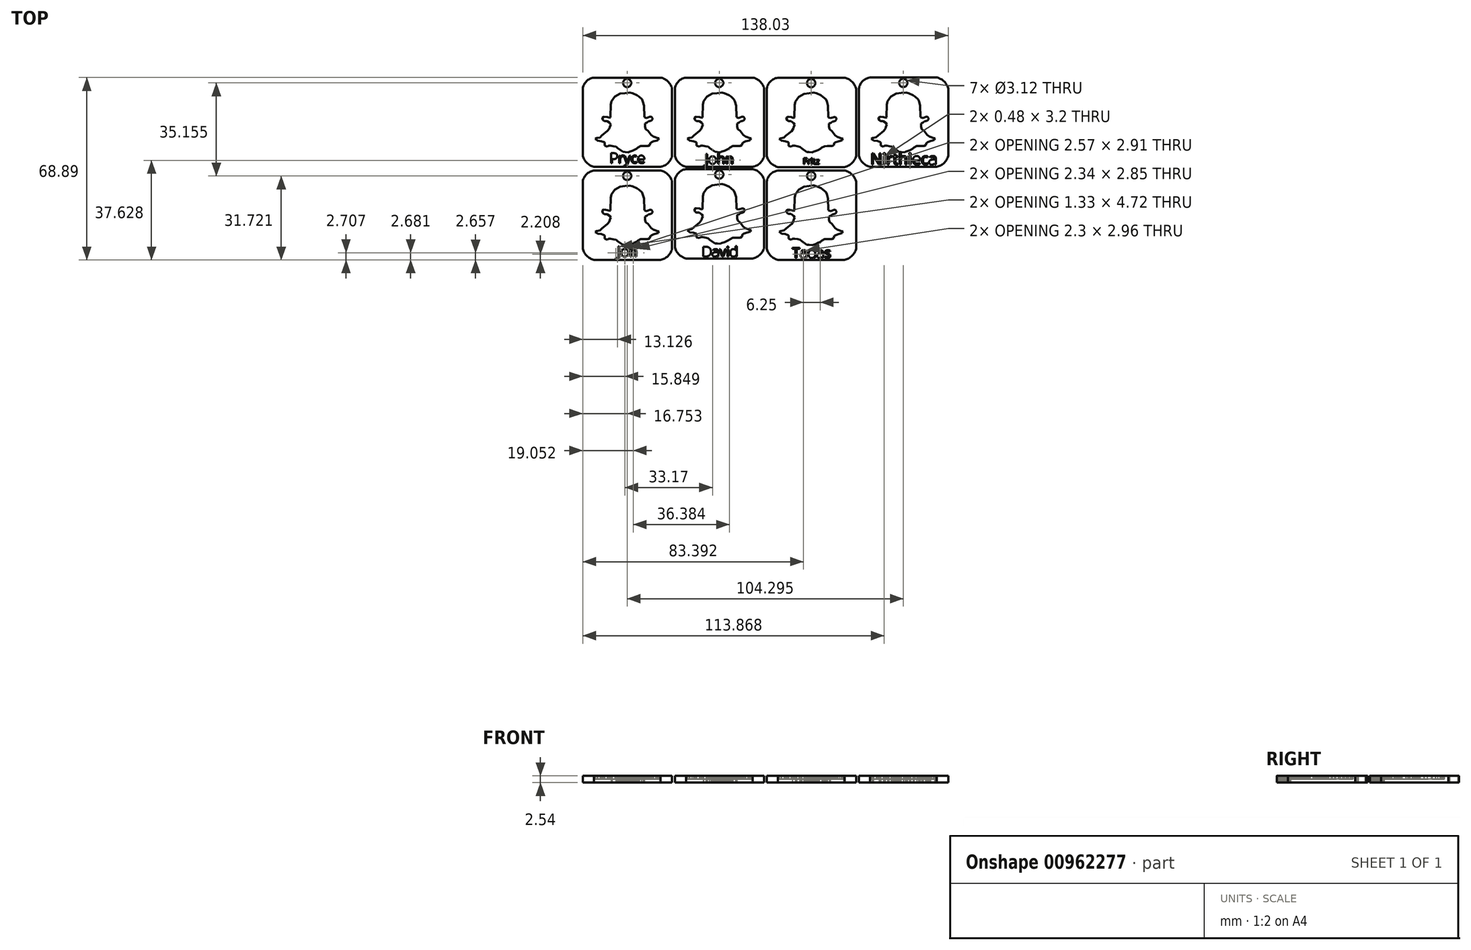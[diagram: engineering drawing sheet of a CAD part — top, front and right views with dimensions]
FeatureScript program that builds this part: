
annotation { "Feature Type Name" : "Feature", "Feature Type Description" : "" }
export const myFeature = defineFeature(function(context is Context, id is Id, definition is map)
    precondition{}
    {
        {
            var Q0;
            Q0=qCreatedBy(makeId("Top.planeOp"),FACE);
            var sketch = newSketch(context, id + "F0", { "sketchPlane" : qUnion([Q0])});
            skPoint(sketch, "E0.middle", {"position": v(-58.3, 36.23) * mm});
            skPoint(sketch, "E1.middle", {"position": v(-58.18, 29.07) * mm});
            skLineSegment(sketch, "E2", {"start": v(-64.66, 30.3) * mm, "end": v(-64.47, 34.86) * mm});
            skLineSegment(sketch, "E3", {"start": v(-64.47, 34.86) * mm, "end": v(-64.28, 36.1) * mm});
            skLineSegment(sketch, "E4", {"start": v(-64.28, 36.1) * mm, "end": v(-62.95, 37.88) * mm});
            skLineSegment(sketch, "E5", {"start": v(-62.95, 37.88) * mm, "end": v(-60.96, 39.02) * mm});
            skLineSegment(sketch, "E6", {"start": v(-60.96, 39.02) * mm, "end": v(-59.1, 39.25) * mm});
            skLineSegment(sketch, "E7", {"start": v(-59.1, 39.25) * mm, "end": v(-57.35, 39.47) * mm});
            skLineSegment(sketch, "E8", {"start": v(-57.35, 39.47) * mm, "end": v(-56.3, 39.2) * mm});
            skLineSegment(sketch, "E9", {"start": v(-56.3, 39.2) * mm, "end": v(-54.6, 38.45) * mm});
            skLineSegment(sketch, "E10", {"start": v(-54.6, 38.45) * mm, "end": v(-53.83, 37.88) * mm});
            skLineSegment(sketch, "E11", {"start": v(-53.83, 37.88) * mm, "end": v(-52.74, 36.93) * mm});
            skLineSegment(sketch, "E12", {"start": v(-52.74, 36.93) * mm, "end": v(-52.36, 36.1) * mm});
            skLineSegment(sketch, "E13", {"start": v(-52.36, 36.1) * mm, "end": v(-51.94, 34.53) * mm});
            skLineSegment(sketch, "E14", {"start": v(-51.94, 34.53) * mm, "end": v(-51.94, 33.03) * mm});
            skLineSegment(sketch, "E15", {"start": v(-51.94, 33.03) * mm, "end": v(-51.84, 31.8) * mm});
            skLineSegment(sketch, "E16", {"start": v(-51.84, 31.8) * mm, "end": v(-51.84, 30.61) * mm});
            skLineSegment(sketch, "E17", {"start": v(-51.84, 30.61) * mm, "end": v(-51.84, 30.14) * mm});
            skLineSegment(sketch, "E18", {"start": v(-51.84, 30.14) * mm, "end": v(-50.99, 29.8) * mm});
            skLineSegment(sketch, "E19", {"start": v(-50.99, 29.8) * mm, "end": v(-49.7, 30.28) * mm});
            skLineSegment(sketch, "E20", {"start": v(-49.7, 30.28) * mm, "end": v(-49.18, 30.28) * mm});
            skLineSegment(sketch, "E21", {"start": v(-49.18, 30.28) * mm, "end": v(-48.8, 29.8) * mm});
            skLineSegment(sketch, "E22", {"start": v(-48.8, 29.8) * mm, "end": v(-48.8, 29.3) * mm});
            skLineSegment(sketch, "E23", {"start": v(-48.8, 29.3) * mm, "end": v(-49.14, 28.9) * mm});
            skLineSegment(sketch, "E24", {"start": v(-49.14, 28.9) * mm, "end": v(-49.73, 28.63) * mm});
            skLineSegment(sketch, "E25", {"start": v(-49.73, 28.63) * mm, "end": v(-50.14, 28.63) * mm});
            skLineSegment(sketch, "E26", {"start": v(-50.14, 28.63) * mm, "end": v(-50.82, 28.13) * mm});
            skLineSegment(sketch, "E27", {"start": v(-50.82, 28.13) * mm, "end": v(-51.57, 27.77) * mm});
            skLineSegment(sketch, "E28", {"start": v(-51.57, 27.77) * mm, "end": v(-51.57, 27.21) * mm});
            skLineSegment(sketch, "E29", {"start": v(-51.57, 27.21) * mm, "end": v(-51.57, 26.48) * mm});
            skLineSegment(sketch, "E30", {"start": v(-51.57, 26.48) * mm, "end": v(-51.28, 25.62) * mm});
            skLineSegment(sketch, "E31", {"start": v(-51.28, 25.62) * mm, "end": v(-50.37, 24.96) * mm});
            skLineSegment(sketch, "E32", {"start": v(-50.37, 24.96) * mm, "end": v(-49.26, 23.43) * mm});
            skLineSegment(sketch, "E33", {"start": v(-49.26, 23.43) * mm, "end": v(-48.4, 22.8) * mm});
            skLineSegment(sketch, "E34", {"start": v(-48.4, 22.8) * mm, "end": v(-47.65, 22.5) * mm});
            skLineSegment(sketch, "E35", {"start": v(-47.65, 22.5) * mm, "end": v(-46.73, 22.16) * mm});
            skLineSegment(sketch, "E36", {"start": v(-46.73, 22.16) * mm, "end": v(-46.2, 22.16) * mm});
            skLineSegment(sketch, "E37", {"start": v(-46.2, 22.16) * mm, "end": v(-46.46, 21.8) * mm});
            skLineSegment(sketch, "E38", {"start": v(-46.46, 21.8) * mm, "end": v(-46.58, 21.51) * mm});
            skLineSegment(sketch, "E39", {"start": v(-46.58, 21.51) * mm, "end": v(-47.04, 21.34) * mm});
            skLineSegment(sketch, "E40", {"start": v(-47.04, 21.34) * mm, "end": v(-48.32, 21.02) * mm});
            skLineSegment(sketch, "E41", {"start": v(-48.32, 21.02) * mm, "end": v(-49.1, 20.65) * mm});
            skLineSegment(sketch, "E42", {"start": v(-49.1, 20.65) * mm, "end": v(-49.54, 20.43) * mm});
            skLineSegment(sketch, "E43", {"start": v(-49.54, 20.43) * mm, "end": v(-49.73, 19.58) * mm});
            skLineSegment(sketch, "E44", {"start": v(-49.73, 19.58) * mm, "end": v(-50.37, 19.25) * mm});
            skLineSegment(sketch, "E45", {"start": v(-50.37, 19.25) * mm, "end": v(-52.22, 19.25) * mm});
            skLineSegment(sketch, "E46", {"start": v(-52.22, 19.25) * mm, "end": v(-53.17, 19.24) * mm});
            skLineSegment(sketch, "E47", {"start": v(-53.17, 19.24) * mm, "end": v(-54.37, 18.62) * mm});
            skLineSegment(sketch, "E48", {"start": v(-54.37, 18.62) * mm, "end": v(-54.76, 18.25) * mm});
            skLineSegment(sketch, "E49", {"start": v(-54.76, 18.25) * mm, "end": v(-55.68, 17.76) * mm});
            skLineSegment(sketch, "E50", {"start": v(-55.68, 17.76) * mm, "end": v(-56.25, 17.49) * mm});
            skLineSegment(sketch, "E51", {"start": v(-56.25, 17.49) * mm, "end": v(-57.44, 17.1) * mm});
            skLineSegment(sketch, "E52", {"start": v(-57.44, 17.1) * mm, "end": v(-57.85, 16.9) * mm});
            skLineSegment(sketch, "E53", {"start": v(-57.85, 16.9) * mm, "end": v(-59.06, 17.01) * mm});
            skLineSegment(sketch, "E54", {"start": v(-59.06, 17.01) * mm, "end": v(-59.96, 17.06) * mm});
            skLineSegment(sketch, "E55", {"start": v(-59.96, 17.06) * mm, "end": v(-60.86, 17.71) * mm});
            skLineSegment(sketch, "E56", {"start": v(-60.86, 17.71) * mm, "end": v(-61.9, 18.48) * mm});
            skLineSegment(sketch, "E57", {"start": v(-61.9, 18.48) * mm, "end": v(-62.47, 18.96) * mm});
            skLineSegment(sketch, "E58", {"start": v(-62.47, 18.96) * mm, "end": v(-63.4, 19.15) * mm});
            skLineSegment(sketch, "E59", {"start": v(-63.4, 19.15) * mm, "end": v(-64.56, 19.38) * mm});
            skLineSegment(sketch, "E60", {"start": v(-64.56, 19.38) * mm, "end": v(-65.42, 19.38) * mm});
            skLineSegment(sketch, "E61", {"start": v(-65.42, 19.38) * mm, "end": v(-65.8, 19) * mm});
            skLineSegment(sketch, "E62", {"start": v(-65.8, 19) * mm, "end": v(-66.84, 19.36) * mm});
            skLineSegment(sketch, "E63", {"start": v(-66.84, 19.36) * mm, "end": v(-66.84, 20.65) * mm});
            skLineSegment(sketch, "E64", {"start": v(-66.84, 20.65) * mm, "end": v(-68.03, 21.1) * mm});
            skLineSegment(sketch, "E65", {"start": v(-68.03, 21.1) * mm, "end": v(-69.43, 21.28) * mm});
            skLineSegment(sketch, "E66", {"start": v(-69.43, 21.28) * mm, "end": v(-70.32, 21.94) * mm});
            skLineSegment(sketch, "E67", {"start": v(-70.32, 21.94) * mm, "end": v(-69.71, 22.25) * mm});
            skLineSegment(sketch, "E68", {"start": v(-69.71, 22.25) * mm, "end": v(-68.62, 22.5) * mm});
            skLineSegment(sketch, "E69", {"start": v(-68.62, 22.5) * mm, "end": v(-67.86, 23.18) * mm});
            skLineSegment(sketch, "E70", {"start": v(-67.86, 23.18) * mm, "end": v(-65.73, 24.96) * mm});
            skLineSegment(sketch, "E71", {"start": v(-65.73, 24.96) * mm, "end": v(-65.05, 25.89) * mm});
            skLineSegment(sketch, "E72", {"start": v(-65.05, 25.89) * mm, "end": v(-64.92, 26.41) * mm});
            skLineSegment(sketch, "E73", {"start": v(-64.92, 26.41) * mm, "end": v(-64.54, 27.31) * mm});
            skLineSegment(sketch, "E74", {"start": v(-64.54, 27.31) * mm, "end": v(-64.88, 27.97) * mm});
            skLineSegment(sketch, "E75", {"start": v(-64.88, 27.97) * mm, "end": v(-65.86, 28.68) * mm});
            skLineSegment(sketch, "E76", {"start": v(-65.86, 28.68) * mm, "end": v(-66.89, 28.68) * mm});
            skLineSegment(sketch, "E77", {"start": v(-66.89, 28.68) * mm, "end": v(-67.37, 29.03) * mm});
            skLineSegment(sketch, "E78", {"start": v(-67.37, 29.03) * mm, "end": v(-67.67, 29.69) * mm});
            skLineSegment(sketch, "E79", {"start": v(-67.67, 29.69) * mm, "end": v(-67.67, 29.97) * mm});
            skLineSegment(sketch, "E80", {"start": v(-67.67, 29.97) * mm, "end": v(-66.97, 30.34) * mm});
            skLineSegment(sketch, "E81", {"start": v(-66.97, 30.34) * mm, "end": v(-65.8, 30.19) * mm});
            skLineSegment(sketch, "E82", {"start": v(-65.8, 30.19) * mm, "end": v(-64.88, 29.9) * mm});
            skLineSegment(sketch, "E83", {"start": v(-64.88, 29.9) * mm, "end": v(-64.58, 30.06) * mm});
            skLineSegment(sketch, "E84", {"start": v(-64.58, 30.06) * mm, "end": v(-64.66, 30.3) * mm});
            skLineSegment(sketch, "E85", {"start": v(-41.32, 40.96) * mm, "end": v(-41.32, 15.52) * mm});
            skArc(sketch, "E86", {"start": v(-45.7, 11.36) * mm, "mid": v(-42.9, 12.8) * mm, "end": v(-41.32, 15.52) * mm});
            skLineSegment(sketch, "E87", {"start": v(-45.7, 11.36) * mm, "end": v(-70.84, 11.36) * mm});
            skArc(sketch, "E88", {"start": v(-75.06, 15.5) * mm, "mid": v(-73.51, 12.86) * mm, "end": v(-70.84, 11.36) * mm});
            skLineSegment(sketch, "E89", {"start": v(-75.06, 15.5) * mm, "end": v(-75.06, 41) * mm});
            skArc(sketch, "E90", {"start": v(-70.93, 45.1) * mm, "mid": v(-73.67, 43.72) * mm, "end": v(-75.06, 41) * mm});
            skLineSegment(sketch, "E91", {"start": v(-70.93, 45.1) * mm, "end": v(-45.53, 45.1) * mm});
            skArc(sketch, "E92", {"start": v(-41.32, 40.96) * mm, "mid": v(-42.85, 43.61) * mm, "end": v(-45.53, 45.1) * mm});
            skCircle(sketch, "E93", {"center": v(-58.3, 43.08) * mm, "radius": 1.56 * mm});
            skText(sketch, "E94", { "text": "Pryce", "fontName": "OpenSans-Regular.ttf"});
            skLineSegment(sketch, "E95", {"start": v(-58.19, 31.88) * mm, "end": v(-58.18, 29.07) * mm, "construction": true});
            skLineSegment(sketch, "E96", {"start": v(-58.18, 29.07) * mm, "end": v(-58.18, 11.36) * mm});
            skPoint(sketch, "E97.middle", {"position": v(-58.3, 1.1) * mm});
            skPoint(sketch, "E98.middle", {"position": v(-58.18, -6.06) * mm});
            skLineSegment(sketch, "E99", {"start": v(-64.66, -4.83) * mm, "end": v(-64.47, -0.27) * mm});
            skLineSegment(sketch, "E100", {"start": v(-64.47, -0.27) * mm, "end": v(-64.28, 0.96) * mm});
            skLineSegment(sketch, "E101", {"start": v(-64.28, 0.96) * mm, "end": v(-62.95, 2.74) * mm});
            skLineSegment(sketch, "E102", {"start": v(-62.95, 2.74) * mm, "end": v(-60.96, 3.88) * mm});
            skLineSegment(sketch, "E103", {"start": v(-60.96, 3.88) * mm, "end": v(-59.1, 4.12) * mm});
            skLineSegment(sketch, "E104", {"start": v(-59.1, 4.12) * mm, "end": v(-57.35, 4.33) * mm});
            skLineSegment(sketch, "E105", {"start": v(-57.35, 4.33) * mm, "end": v(-56.3, 4.07) * mm});
            skLineSegment(sketch, "E106", {"start": v(-56.3, 4.07) * mm, "end": v(-54.6, 3.3) * mm});
            skLineSegment(sketch, "E107", {"start": v(-54.6, 3.3) * mm, "end": v(-53.83, 2.74) * mm});
            skLineSegment(sketch, "E108", {"start": v(-53.83, 2.74) * mm, "end": v(-52.74, 1.8) * mm});
            skLineSegment(sketch, "E109", {"start": v(-52.74, 1.8) * mm, "end": v(-52.36, 0.96) * mm});
            skLineSegment(sketch, "E110", {"start": v(-52.36, 0.96) * mm, "end": v(-51.94, -0.6) * mm});
            skLineSegment(sketch, "E111", {"start": v(-51.94, -0.6) * mm, "end": v(-51.94, -2.1) * mm});
            skLineSegment(sketch, "E112", {"start": v(-51.94, -2.1) * mm, "end": v(-51.84, -3.34) * mm});
            skLineSegment(sketch, "E113", {"start": v(-51.84, -3.34) * mm, "end": v(-51.84, -4.52) * mm});
            skLineSegment(sketch, "E114", {"start": v(-51.84, -4.52) * mm, "end": v(-51.84, -5) * mm});
            skLineSegment(sketch, "E115", {"start": v(-51.84, -5) * mm, "end": v(-50.99, -5.33) * mm});
            skLineSegment(sketch, "E116", {"start": v(-50.99, -5.33) * mm, "end": v(-49.7, -4.86) * mm});
            skLineSegment(sketch, "E117", {"start": v(-49.7, -4.86) * mm, "end": v(-49.18, -4.86) * mm});
            skLineSegment(sketch, "E118", {"start": v(-49.18, -4.86) * mm, "end": v(-48.8, -5.33) * mm});
            skLineSegment(sketch, "E119", {"start": v(-48.8, -5.33) * mm, "end": v(-48.8, -5.84) * mm});
            skLineSegment(sketch, "E120", {"start": v(-48.8, -5.84) * mm, "end": v(-49.14, -6.24) * mm});
            skLineSegment(sketch, "E121", {"start": v(-49.14, -6.24) * mm, "end": v(-49.73, -6.51) * mm});
            skLineSegment(sketch, "E122", {"start": v(-49.73, -6.51) * mm, "end": v(-50.14, -6.51) * mm});
            skLineSegment(sketch, "E123", {"start": v(-50.14, -6.51) * mm, "end": v(-50.82, -7) * mm});
            skLineSegment(sketch, "E124", {"start": v(-50.82, -7) * mm, "end": v(-51.57, -7.37) * mm});
            skLineSegment(sketch, "E125", {"start": v(-51.57, -7.37) * mm, "end": v(-51.57, -7.93) * mm});
            skLineSegment(sketch, "E126", {"start": v(-51.57, -7.93) * mm, "end": v(-51.57, -8.65) * mm});
            skLineSegment(sketch, "E127", {"start": v(-51.57, -8.65) * mm, "end": v(-51.28, -9.51) * mm});
            skLineSegment(sketch, "E128", {"start": v(-51.28, -9.51) * mm, "end": v(-50.37, -10.18) * mm});
            skLineSegment(sketch, "E129", {"start": v(-50.37, -10.18) * mm, "end": v(-49.26, -11.71) * mm});
            skLineSegment(sketch, "E130", {"start": v(-49.26, -11.71) * mm, "end": v(-48.4, -12.34) * mm});
            skLineSegment(sketch, "E131", {"start": v(-48.4, -12.34) * mm, "end": v(-47.65, -12.63) * mm});
            skLineSegment(sketch, "E132", {"start": v(-47.65, -12.63) * mm, "end": v(-46.73, -12.97) * mm});
            skLineSegment(sketch, "E133", {"start": v(-46.73, -12.97) * mm, "end": v(-46.2, -12.97) * mm});
            skLineSegment(sketch, "E134", {"start": v(-46.2, -12.97) * mm, "end": v(-46.46, -13.34) * mm});
            skLineSegment(sketch, "E135", {"start": v(-46.46, -13.34) * mm, "end": v(-46.58, -13.62) * mm});
            skLineSegment(sketch, "E136", {"start": v(-46.58, -13.62) * mm, "end": v(-47.04, -13.8) * mm});
            skLineSegment(sketch, "E137", {"start": v(-47.04, -13.8) * mm, "end": v(-48.32, -14.12) * mm});
            skLineSegment(sketch, "E138", {"start": v(-48.32, -14.12) * mm, "end": v(-49.1, -14.48) * mm});
            skLineSegment(sketch, "E139", {"start": v(-49.1, -14.48) * mm, "end": v(-49.54, -14.71) * mm});
            skLineSegment(sketch, "E140", {"start": v(-49.54, -14.71) * mm, "end": v(-49.73, -15.55) * mm});
            skLineSegment(sketch, "E141", {"start": v(-49.73, -15.55) * mm, "end": v(-50.37, -15.88) * mm});
            skLineSegment(sketch, "E142", {"start": v(-50.37, -15.88) * mm, "end": v(-52.22, -15.88) * mm});
            skLineSegment(sketch, "E143", {"start": v(-52.22, -15.88) * mm, "end": v(-53.17, -15.9) * mm});
            skLineSegment(sketch, "E144", {"start": v(-53.17, -15.9) * mm, "end": v(-54.37, -16.52) * mm});
            skLineSegment(sketch, "E145", {"start": v(-54.37, -16.52) * mm, "end": v(-54.76, -16.9) * mm});
            skLineSegment(sketch, "E146", {"start": v(-54.76, -16.9) * mm, "end": v(-55.68, -17.37) * mm});
            skLineSegment(sketch, "E147", {"start": v(-55.68, -17.37) * mm, "end": v(-56.25, -17.65) * mm});
            skLineSegment(sketch, "E148", {"start": v(-56.25, -17.65) * mm, "end": v(-57.44, -18.03) * mm});
            skLineSegment(sketch, "E149", {"start": v(-57.44, -18.03) * mm, "end": v(-57.85, -18.25) * mm});
            skLineSegment(sketch, "E150", {"start": v(-57.85, -18.25) * mm, "end": v(-59.06, -18.13) * mm});
            skLineSegment(sketch, "E151", {"start": v(-59.06, -18.13) * mm, "end": v(-59.96, -18.08) * mm});
            skLineSegment(sketch, "E152", {"start": v(-59.96, -18.08) * mm, "end": v(-60.86, -17.42) * mm});
            skLineSegment(sketch, "E153", {"start": v(-60.86, -17.42) * mm, "end": v(-61.9, -16.66) * mm});
            skLineSegment(sketch, "E154", {"start": v(-61.9, -16.66) * mm, "end": v(-62.47, -16.18) * mm});
            skLineSegment(sketch, "E155", {"start": v(-62.47, -16.18) * mm, "end": v(-63.4, -15.99) * mm});
            skLineSegment(sketch, "E156", {"start": v(-63.4, -15.99) * mm, "end": v(-64.56, -15.75) * mm});
            skLineSegment(sketch, "E157", {"start": v(-64.56, -15.75) * mm, "end": v(-65.42, -15.75) * mm});
            skLineSegment(sketch, "E158", {"start": v(-65.42, -15.75) * mm, "end": v(-65.8, -16.13) * mm});
            skLineSegment(sketch, "E159", {"start": v(-65.8, -16.13) * mm, "end": v(-66.84, -15.78) * mm});
            skLineSegment(sketch, "E160", {"start": v(-66.84, -15.78) * mm, "end": v(-66.84, -14.48) * mm});
            skLineSegment(sketch, "E161", {"start": v(-66.84, -14.48) * mm, "end": v(-68.03, -14.04) * mm});
            skLineSegment(sketch, "E162", {"start": v(-68.03, -14.04) * mm, "end": v(-69.43, -13.85) * mm});
            skLineSegment(sketch, "E163", {"start": v(-69.43, -13.85) * mm, "end": v(-70.32, -13.2) * mm});
            skLineSegment(sketch, "E164", {"start": v(-70.32, -13.2) * mm, "end": v(-69.71, -12.88) * mm});
            skLineSegment(sketch, "E165", {"start": v(-69.71, -12.88) * mm, "end": v(-68.62, -12.64) * mm});
            skLineSegment(sketch, "E166", {"start": v(-68.62, -12.64) * mm, "end": v(-67.86, -11.95) * mm});
            skLineSegment(sketch, "E167", {"start": v(-67.86, -11.95) * mm, "end": v(-65.73, -10.18) * mm});
            skLineSegment(sketch, "E168", {"start": v(-65.73, -10.18) * mm, "end": v(-65.05, -9.25) * mm});
            skLineSegment(sketch, "E169", {"start": v(-65.05, -9.25) * mm, "end": v(-64.92, -8.73) * mm});
            skLineSegment(sketch, "E170", {"start": v(-64.92, -8.73) * mm, "end": v(-64.54, -7.82) * mm});
            skLineSegment(sketch, "E171", {"start": v(-64.54, -7.82) * mm, "end": v(-64.88, -7.17) * mm});
            skLineSegment(sketch, "E172", {"start": v(-64.88, -7.17) * mm, "end": v(-65.86, -6.45) * mm});
            skLineSegment(sketch, "E173", {"start": v(-65.86, -6.45) * mm, "end": v(-66.89, -6.45) * mm});
            skLineSegment(sketch, "E174", {"start": v(-66.89, -6.45) * mm, "end": v(-67.37, -6.1) * mm});
            skLineSegment(sketch, "E175", {"start": v(-67.37, -6.1) * mm, "end": v(-67.67, -5.45) * mm});
            skLineSegment(sketch, "E176", {"start": v(-67.67, -5.45) * mm, "end": v(-67.67, -5.16) * mm});
            skLineSegment(sketch, "E177", {"start": v(-67.67, -5.16) * mm, "end": v(-66.97, -4.8) * mm});
            skLineSegment(sketch, "E178", {"start": v(-66.97, -4.8) * mm, "end": v(-65.8, -4.95) * mm});
            skLineSegment(sketch, "E179", {"start": v(-65.8, -4.95) * mm, "end": v(-64.88, -5.24) * mm});
            skLineSegment(sketch, "E180", {"start": v(-64.88, -5.24) * mm, "end": v(-64.58, -5.08) * mm});
            skLineSegment(sketch, "E181", {"start": v(-64.58, -5.08) * mm, "end": v(-64.66, -4.83) * mm});
            skLineSegment(sketch, "E182", {"start": v(-41.32, 5.82) * mm, "end": v(-41.32, -19.62) * mm});
            skArc(sketch, "E183", {"start": v(-45.7, -23.78) * mm, "mid": v(-42.9, -22.34) * mm, "end": v(-41.32, -19.62) * mm});
            skLineSegment(sketch, "E184", {"start": v(-45.7, -23.78) * mm, "end": v(-70.84, -23.78) * mm});
            skArc(sketch, "E185", {"start": v(-75.06, -19.63) * mm, "mid": v(-73.51, -22.28) * mm, "end": v(-70.84, -23.78) * mm});
            skLineSegment(sketch, "E186", {"start": v(-75.06, -19.63) * mm, "end": v(-75.06, 5.85) * mm});
            skArc(sketch, "E187", {"start": v(-70.93, 9.96) * mm, "mid": v(-73.67, 8.58) * mm, "end": v(-75.06, 5.85) * mm});
            skLineSegment(sketch, "E188", {"start": v(-70.93, 9.96) * mm, "end": v(-45.53, 9.96) * mm});
            skArc(sketch, "E189", {"start": v(-41.32, 5.82) * mm, "mid": v(-42.85, 8.47) * mm, "end": v(-45.53, 9.96) * mm});
            skCircle(sketch, "E190", {"center": v(-58.3, 7.94) * mm, "radius": 1.56 * mm});
            skLineSegment(sketch, "E191", {"start": v(-58.19, -3.26) * mm, "end": v(-58.18, -6.06) * mm, "construction": true});
            skLineSegment(sketch, "E192", {"start": v(-58.18, -6.06) * mm, "end": v(-58.18, -23.78) * mm});
            skText(sketch, "E193", { "text": "Jon", "fontName": "OpenSans-Regular.ttf"});
            skPoint(sketch, "E194.middle", {"position": v(-23.52, 36.23) * mm});
            skPoint(sketch, "E195.middle", {"position": v(-23.39, 29.07) * mm});
            skLineSegment(sketch, "E196", {"start": v(-29.87, 30.3) * mm, "end": v(-29.68, 34.86) * mm});
            skLineSegment(sketch, "E197", {"start": v(-29.68, 34.86) * mm, "end": v(-29.5, 36.1) * mm});
            skLineSegment(sketch, "E198", {"start": v(-29.5, 36.1) * mm, "end": v(-28.16, 37.88) * mm});
            skLineSegment(sketch, "E199", {"start": v(-28.16, 37.88) * mm, "end": v(-26.17, 39.02) * mm});
            skLineSegment(sketch, "E200", {"start": v(-26.17, 39.02) * mm, "end": v(-24.32, 39.25) * mm});
            skLineSegment(sketch, "E201", {"start": v(-24.32, 39.25) * mm, "end": v(-22.56, 39.47) * mm});
            skLineSegment(sketch, "E202", {"start": v(-22.56, 39.47) * mm, "end": v(-21.51, 39.2) * mm});
            skLineSegment(sketch, "E203", {"start": v(-21.51, 39.2) * mm, "end": v(-19.8, 38.45) * mm});
            skLineSegment(sketch, "E204", {"start": v(-19.8, 38.45) * mm, "end": v(-19.05, 37.88) * mm});
            skLineSegment(sketch, "E205", {"start": v(-19.05, 37.88) * mm, "end": v(-17.95, 36.93) * mm});
            skLineSegment(sketch, "E206", {"start": v(-17.95, 36.93) * mm, "end": v(-17.57, 36.1) * mm});
            skLineSegment(sketch, "E207", {"start": v(-17.57, 36.1) * mm, "end": v(-17.15, 34.53) * mm});
            skLineSegment(sketch, "E208", {"start": v(-17.15, 34.53) * mm, "end": v(-17.15, 33.03) * mm});
            skLineSegment(sketch, "E209", {"start": v(-17.15, 33.03) * mm, "end": v(-17.05, 31.8) * mm});
            skLineSegment(sketch, "E210", {"start": v(-17.05, 31.8) * mm, "end": v(-17.05, 30.61) * mm});
            skLineSegment(sketch, "E211", {"start": v(-17.05, 30.61) * mm, "end": v(-17.05, 30.14) * mm});
            skLineSegment(sketch, "E212", {"start": v(-17.05, 30.14) * mm, "end": v(-16.2, 29.8) * mm});
            skLineSegment(sketch, "E213", {"start": v(-16.2, 29.8) * mm, "end": v(-14.91, 30.28) * mm});
            skLineSegment(sketch, "E214", {"start": v(-14.91, 30.28) * mm, "end": v(-14.4, 30.28) * mm});
            skLineSegment(sketch, "E215", {"start": v(-14.4, 30.28) * mm, "end": v(-14.01, 29.8) * mm});
            skLineSegment(sketch, "E216", {"start": v(-14.01, 29.8) * mm, "end": v(-14.01, 29.3) * mm});
            skLineSegment(sketch, "E217", {"start": v(-14.01, 29.3) * mm, "end": v(-14.35, 28.9) * mm});
            skLineSegment(sketch, "E218", {"start": v(-14.35, 28.9) * mm, "end": v(-14.95, 28.63) * mm});
            skLineSegment(sketch, "E219", {"start": v(-14.95, 28.63) * mm, "end": v(-15.35, 28.63) * mm});
            skLineSegment(sketch, "E220", {"start": v(-15.35, 28.63) * mm, "end": v(-16.03, 28.13) * mm});
            skLineSegment(sketch, "E221", {"start": v(-16.03, 28.13) * mm, "end": v(-16.78, 27.77) * mm});
            skLineSegment(sketch, "E222", {"start": v(-16.78, 27.77) * mm, "end": v(-16.78, 27.21) * mm});
            skLineSegment(sketch, "E223", {"start": v(-16.78, 27.21) * mm, "end": v(-16.78, 26.48) * mm});
            skLineSegment(sketch, "E224", {"start": v(-16.78, 26.48) * mm, "end": v(-16.5, 25.62) * mm});
            skLineSegment(sketch, "E225", {"start": v(-16.5, 25.62) * mm, "end": v(-15.58, 24.96) * mm});
            skLineSegment(sketch, "E226", {"start": v(-15.58, 24.96) * mm, "end": v(-14.47, 23.43) * mm});
            skLineSegment(sketch, "E227", {"start": v(-14.47, 23.43) * mm, "end": v(-13.6, 22.8) * mm});
            skLineSegment(sketch, "E228", {"start": v(-13.6, 22.8) * mm, "end": v(-12.86, 22.5) * mm});
            skLineSegment(sketch, "E229", {"start": v(-12.86, 22.5) * mm, "end": v(-11.94, 22.16) * mm});
            skLineSegment(sketch, "E230", {"start": v(-11.94, 22.16) * mm, "end": v(-11.4, 22.16) * mm});
            skLineSegment(sketch, "E231", {"start": v(-11.4, 22.16) * mm, "end": v(-11.68, 21.8) * mm});
            skLineSegment(sketch, "E232", {"start": v(-11.68, 21.8) * mm, "end": v(-11.8, 21.51) * mm});
            skLineSegment(sketch, "E233", {"start": v(-11.8, 21.51) * mm, "end": v(-12.25, 21.34) * mm});
            skLineSegment(sketch, "E234", {"start": v(-12.25, 21.34) * mm, "end": v(-13.53, 21.02) * mm});
            skLineSegment(sketch, "E235", {"start": v(-13.53, 21.02) * mm, "end": v(-14.31, 20.65) * mm});
            skLineSegment(sketch, "E236", {"start": v(-14.31, 20.65) * mm, "end": v(-14.75, 20.43) * mm});
            skLineSegment(sketch, "E237", {"start": v(-14.75, 20.43) * mm, "end": v(-14.95, 19.58) * mm});
            skLineSegment(sketch, "E238", {"start": v(-14.95, 19.58) * mm, "end": v(-15.58, 19.25) * mm});
            skLineSegment(sketch, "E239", {"start": v(-15.58, 19.25) * mm, "end": v(-17.43, 19.25) * mm});
            skLineSegment(sketch, "E240", {"start": v(-17.43, 19.25) * mm, "end": v(-18.38, 19.24) * mm});
            skLineSegment(sketch, "E241", {"start": v(-18.38, 19.24) * mm, "end": v(-19.58, 18.62) * mm});
            skLineSegment(sketch, "E242", {"start": v(-19.58, 18.62) * mm, "end": v(-19.97, 18.25) * mm});
            skLineSegment(sketch, "E243", {"start": v(-19.97, 18.25) * mm, "end": v(-20.9, 17.76) * mm});
            skLineSegment(sketch, "E244", {"start": v(-20.9, 17.76) * mm, "end": v(-21.47, 17.49) * mm});
            skLineSegment(sketch, "E245", {"start": v(-21.47, 17.49) * mm, "end": v(-22.65, 17.1) * mm});
            skLineSegment(sketch, "E246", {"start": v(-22.65, 17.1) * mm, "end": v(-23.07, 16.9) * mm});
            skLineSegment(sketch, "E247", {"start": v(-23.07, 16.9) * mm, "end": v(-24.27, 17.01) * mm});
            skLineSegment(sketch, "E248", {"start": v(-24.27, 17.01) * mm, "end": v(-25.17, 17.06) * mm});
            skLineSegment(sketch, "E249", {"start": v(-25.17, 17.06) * mm, "end": v(-26.07, 17.71) * mm});
            skLineSegment(sketch, "E250", {"start": v(-26.07, 17.71) * mm, "end": v(-27.11, 18.48) * mm});
            skLineSegment(sketch, "E251", {"start": v(-27.11, 18.48) * mm, "end": v(-27.68, 18.96) * mm});
            skLineSegment(sketch, "E252", {"start": v(-27.68, 18.96) * mm, "end": v(-28.61, 19.15) * mm});
            skLineSegment(sketch, "E253", {"start": v(-28.61, 19.15) * mm, "end": v(-29.77, 19.38) * mm});
            skLineSegment(sketch, "E254", {"start": v(-29.77, 19.38) * mm, "end": v(-30.63, 19.38) * mm});
            skLineSegment(sketch, "E255", {"start": v(-30.63, 19.38) * mm, "end": v(-31, 19) * mm});
            skLineSegment(sketch, "E256", {"start": v(-31, 19) * mm, "end": v(-32.05, 19.36) * mm});
            skLineSegment(sketch, "E257", {"start": v(-32.05, 19.36) * mm, "end": v(-32.05, 20.65) * mm});
            skLineSegment(sketch, "E258", {"start": v(-32.05, 20.65) * mm, "end": v(-33.24, 21.1) * mm});
            skLineSegment(sketch, "E259", {"start": v(-33.24, 21.1) * mm, "end": v(-34.64, 21.28) * mm});
            skLineSegment(sketch, "E260", {"start": v(-34.64, 21.28) * mm, "end": v(-35.53, 21.94) * mm});
            skLineSegment(sketch, "E261", {"start": v(-35.53, 21.94) * mm, "end": v(-34.92, 22.25) * mm});
            skLineSegment(sketch, "E262", {"start": v(-34.92, 22.25) * mm, "end": v(-33.83, 22.5) * mm});
            skLineSegment(sketch, "E263", {"start": v(-33.83, 22.5) * mm, "end": v(-33.07, 23.18) * mm});
            skLineSegment(sketch, "E264", {"start": v(-33.07, 23.18) * mm, "end": v(-30.94, 24.96) * mm});
            skLineSegment(sketch, "E265", {"start": v(-30.94, 24.96) * mm, "end": v(-30.26, 25.89) * mm});
            skLineSegment(sketch, "E266", {"start": v(-30.26, 25.89) * mm, "end": v(-30.13, 26.41) * mm});
            skLineSegment(sketch, "E267", {"start": v(-30.13, 26.41) * mm, "end": v(-29.75, 27.31) * mm});
            skLineSegment(sketch, "E268", {"start": v(-29.75, 27.31) * mm, "end": v(-30.1, 27.97) * mm});
            skLineSegment(sketch, "E269", {"start": v(-30.1, 27.97) * mm, "end": v(-31.07, 28.68) * mm});
            skLineSegment(sketch, "E270", {"start": v(-31.07, 28.68) * mm, "end": v(-32.1, 28.68) * mm});
            skLineSegment(sketch, "E271", {"start": v(-32.1, 28.68) * mm, "end": v(-32.58, 29.03) * mm});
            skLineSegment(sketch, "E272", {"start": v(-32.58, 29.03) * mm, "end": v(-32.88, 29.69) * mm});
            skLineSegment(sketch, "E273", {"start": v(-32.88, 29.69) * mm, "end": v(-32.88, 29.97) * mm});
            skLineSegment(sketch, "E274", {"start": v(-32.88, 29.97) * mm, "end": v(-32.18, 30.34) * mm});
            skLineSegment(sketch, "E275", {"start": v(-32.18, 30.34) * mm, "end": v(-31, 30.19) * mm});
            skLineSegment(sketch, "E276", {"start": v(-31, 30.19) * mm, "end": v(-30.1, 29.9) * mm});
            skLineSegment(sketch, "E277", {"start": v(-30.1, 29.9) * mm, "end": v(-29.8, 30.06) * mm});
            skLineSegment(sketch, "E278", {"start": v(-29.8, 30.06) * mm, "end": v(-29.87, 30.3) * mm});
            skLineSegment(sketch, "E279", {"start": v(-6.53, 40.96) * mm, "end": v(-6.53, 15.52) * mm});
            skArc(sketch, "E280", {"start": v(-10.9, 11.36) * mm, "mid": v(-8.1, 12.8) * mm, "end": v(-6.53, 15.52) * mm});
            skLineSegment(sketch, "E281", {"start": v(-10.9, 11.36) * mm, "end": v(-36.05, 11.36) * mm});
            skArc(sketch, "E282", {"start": v(-40.27, 15.5) * mm, "mid": v(-38.72, 12.86) * mm, "end": v(-36.05, 11.36) * mm});
            skLineSegment(sketch, "E283", {"start": v(-40.27, 15.5) * mm, "end": v(-40.27, 41) * mm});
            skArc(sketch, "E284", {"start": v(-36.14, 45.1) * mm, "mid": v(-38.88, 43.72) * mm, "end": v(-40.27, 41) * mm});
            skLineSegment(sketch, "E285", {"start": v(-36.14, 45.1) * mm, "end": v(-10.74, 45.1) * mm});
            skArc(sketch, "E286", {"start": v(-6.53, 40.96) * mm, "mid": v(-8.06, 43.61) * mm, "end": v(-10.74, 45.1) * mm});
            skCircle(sketch, "E287", {"center": v(-23.52, 43.08) * mm, "radius": 1.56 * mm});
            skLineSegment(sketch, "E288", {"start": v(-23.4, 31.88) * mm, "end": v(-23.39, 29.07) * mm, "construction": true});
            skLineSegment(sketch, "E289", {"start": v(-23.39, 29.07) * mm, "end": v(-23.39, 11.36) * mm});
            skText(sketch, "E290", { "text": "John", "fontName": "OpenSans-Regular.ttf"});
            skPoint(sketch, "E291.middle", {"position": v(-23.52, 1.64) * mm});
            skPoint(sketch, "E292.middle", {"position": v(-23.39, -5.52) * mm});
            skLineSegment(sketch, "E293", {"start": v(-29.87, -4.3) * mm, "end": v(-29.68, 0.26) * mm});
            skLineSegment(sketch, "E294", {"start": v(-29.68, 0.26) * mm, "end": v(-29.5, 1.5) * mm});
            skLineSegment(sketch, "E295", {"start": v(-29.5, 1.5) * mm, "end": v(-28.16, 3.28) * mm});
            skLineSegment(sketch, "E296", {"start": v(-28.16, 3.28) * mm, "end": v(-26.17, 4.42) * mm});
            skLineSegment(sketch, "E297", {"start": v(-26.17, 4.42) * mm, "end": v(-24.32, 4.66) * mm});
            skLineSegment(sketch, "E298", {"start": v(-24.32, 4.66) * mm, "end": v(-22.56, 4.87) * mm});
            skLineSegment(sketch, "E299", {"start": v(-22.56, 4.87) * mm, "end": v(-21.51, 4.6) * mm});
            skLineSegment(sketch, "E300", {"start": v(-21.51, 4.6) * mm, "end": v(-19.8, 3.85) * mm});
            skLineSegment(sketch, "E301", {"start": v(-19.8, 3.85) * mm, "end": v(-19.05, 3.28) * mm});
            skLineSegment(sketch, "E302", {"start": v(-19.05, 3.28) * mm, "end": v(-17.95, 2.33) * mm});
            skLineSegment(sketch, "E303", {"start": v(-17.95, 2.33) * mm, "end": v(-17.57, 1.5) * mm});
            skLineSegment(sketch, "E304", {"start": v(-17.57, 1.5) * mm, "end": v(-17.15, -0.07) * mm});
            skLineSegment(sketch, "E305", {"start": v(-17.15, -0.07) * mm, "end": v(-17.15, -1.56) * mm});
            skLineSegment(sketch, "E306", {"start": v(-17.15, -1.56) * mm, "end": v(-17.05, -2.8) * mm});
            skLineSegment(sketch, "E307", {"start": v(-17.05, -2.8) * mm, "end": v(-17.05, -3.98) * mm});
            skLineSegment(sketch, "E308", {"start": v(-17.05, -3.98) * mm, "end": v(-17.05, -4.46) * mm});
            skLineSegment(sketch, "E309", {"start": v(-17.05, -4.46) * mm, "end": v(-16.2, -4.8) * mm});
            skLineSegment(sketch, "E310", {"start": v(-16.2, -4.8) * mm, "end": v(-14.91, -4.32) * mm});
            skLineSegment(sketch, "E311", {"start": v(-14.91, -4.32) * mm, "end": v(-14.4, -4.32) * mm});
            skLineSegment(sketch, "E312", {"start": v(-14.4, -4.32) * mm, "end": v(-14.01, -4.8) * mm});
            skLineSegment(sketch, "E313", {"start": v(-14.01, -4.8) * mm, "end": v(-14.01, -5.3) * mm});
            skLineSegment(sketch, "E314", {"start": v(-14.01, -5.3) * mm, "end": v(-14.35, -5.7) * mm});
            skLineSegment(sketch, "E315", {"start": v(-14.35, -5.7) * mm, "end": v(-14.95, -5.97) * mm});
            skLineSegment(sketch, "E316", {"start": v(-14.95, -5.97) * mm, "end": v(-15.35, -5.97) * mm});
            skLineSegment(sketch, "E317", {"start": v(-15.35, -5.97) * mm, "end": v(-16.03, -6.47) * mm});
            skLineSegment(sketch, "E318", {"start": v(-16.03, -6.47) * mm, "end": v(-16.78, -6.83) * mm});
            skLineSegment(sketch, "E319", {"start": v(-16.78, -6.83) * mm, "end": v(-16.78, -7.39) * mm});
            skLineSegment(sketch, "E320", {"start": v(-16.78, -7.39) * mm, "end": v(-16.78, -8.11) * mm});
            skLineSegment(sketch, "E321", {"start": v(-16.78, -8.11) * mm, "end": v(-16.5, -8.97) * mm});
            skLineSegment(sketch, "E322", {"start": v(-16.5, -8.97) * mm, "end": v(-15.58, -9.64) * mm});
            skLineSegment(sketch, "E323", {"start": v(-15.58, -9.64) * mm, "end": v(-14.47, -11.17) * mm});
            skLineSegment(sketch, "E324", {"start": v(-14.47, -11.17) * mm, "end": v(-13.6, -11.8) * mm});
            skLineSegment(sketch, "E325", {"start": v(-13.6, -11.8) * mm, "end": v(-12.86, -12.09) * mm});
            skLineSegment(sketch, "E326", {"start": v(-12.86, -12.09) * mm, "end": v(-11.94, -12.43) * mm});
            skLineSegment(sketch, "E327", {"start": v(-11.94, -12.43) * mm, "end": v(-11.4, -12.43) * mm});
            skLineSegment(sketch, "E328", {"start": v(-11.4, -12.43) * mm, "end": v(-11.68, -12.8) * mm});
            skLineSegment(sketch, "E329", {"start": v(-11.68, -12.8) * mm, "end": v(-11.8, -13.08) * mm});
            skLineSegment(sketch, "E330", {"start": v(-11.8, -13.08) * mm, "end": v(-12.25, -13.26) * mm});
            skLineSegment(sketch, "E331", {"start": v(-12.25, -13.26) * mm, "end": v(-13.53, -13.58) * mm});
            skLineSegment(sketch, "E332", {"start": v(-13.53, -13.58) * mm, "end": v(-14.31, -13.94) * mm});
            skLineSegment(sketch, "E333", {"start": v(-14.31, -13.94) * mm, "end": v(-14.75, -14.17) * mm});
            skLineSegment(sketch, "E334", {"start": v(-14.75, -14.17) * mm, "end": v(-14.95, -15.01) * mm});
            skLineSegment(sketch, "E335", {"start": v(-14.95, -15.01) * mm, "end": v(-15.58, -15.34) * mm});
            skLineSegment(sketch, "E336", {"start": v(-15.58, -15.34) * mm, "end": v(-17.43, -15.34) * mm});
            skLineSegment(sketch, "E337", {"start": v(-17.43, -15.34) * mm, "end": v(-18.38, -15.36) * mm});
            skLineSegment(sketch, "E338", {"start": v(-18.38, -15.36) * mm, "end": v(-19.58, -15.98) * mm});
            skLineSegment(sketch, "E339", {"start": v(-19.58, -15.98) * mm, "end": v(-19.97, -16.35) * mm});
            skLineSegment(sketch, "E340", {"start": v(-19.97, -16.35) * mm, "end": v(-20.9, -16.83) * mm});
            skLineSegment(sketch, "E341", {"start": v(-20.9, -16.83) * mm, "end": v(-21.47, -17.11) * mm});
            skLineSegment(sketch, "E342", {"start": v(-21.47, -17.11) * mm, "end": v(-22.65, -17.5) * mm});
            skLineSegment(sketch, "E343", {"start": v(-22.65, -17.5) * mm, "end": v(-23.07, -17.7) * mm});
            skLineSegment(sketch, "E344", {"start": v(-23.07, -17.7) * mm, "end": v(-24.27, -17.59) * mm});
            skLineSegment(sketch, "E345", {"start": v(-24.27, -17.59) * mm, "end": v(-25.17, -17.54) * mm});
            skLineSegment(sketch, "E346", {"start": v(-25.17, -17.54) * mm, "end": v(-26.07, -16.88) * mm});
            skLineSegment(sketch, "E347", {"start": v(-26.07, -16.88) * mm, "end": v(-27.11, -16.12) * mm});
            skLineSegment(sketch, "E348", {"start": v(-27.11, -16.12) * mm, "end": v(-27.68, -15.64) * mm});
            skLineSegment(sketch, "E349", {"start": v(-27.68, -15.64) * mm, "end": v(-28.61, -15.45) * mm});
            skLineSegment(sketch, "E350", {"start": v(-28.61, -15.45) * mm, "end": v(-29.77, -15.21) * mm});
            skLineSegment(sketch, "E351", {"start": v(-29.77, -15.21) * mm, "end": v(-30.63, -15.21) * mm});
            skLineSegment(sketch, "E352", {"start": v(-30.63, -15.21) * mm, "end": v(-31, -15.6) * mm});
            skLineSegment(sketch, "E353", {"start": v(-31, -15.6) * mm, "end": v(-32.05, -15.24) * mm});
            skLineSegment(sketch, "E354", {"start": v(-32.05, -15.24) * mm, "end": v(-32.05, -13.94) * mm});
            skLineSegment(sketch, "E355", {"start": v(-32.05, -13.94) * mm, "end": v(-33.24, -13.5) * mm});
            skLineSegment(sketch, "E356", {"start": v(-33.24, -13.5) * mm, "end": v(-34.64, -13.31) * mm});
            skLineSegment(sketch, "E357", {"start": v(-34.64, -13.31) * mm, "end": v(-35.53, -12.66) * mm});
            skLineSegment(sketch, "E358", {"start": v(-35.53, -12.66) * mm, "end": v(-34.92, -12.34) * mm});
            skLineSegment(sketch, "E359", {"start": v(-34.92, -12.34) * mm, "end": v(-33.83, -12.1) * mm});
            skLineSegment(sketch, "E360", {"start": v(-33.83, -12.1) * mm, "end": v(-33.07, -11.42) * mm});
            skLineSegment(sketch, "E361", {"start": v(-33.07, -11.42) * mm, "end": v(-30.94, -9.64) * mm});
            skLineSegment(sketch, "E362", {"start": v(-30.94, -9.64) * mm, "end": v(-30.26, -8.71) * mm});
            skLineSegment(sketch, "E363", {"start": v(-30.26, -8.71) * mm, "end": v(-30.13, -8.19) * mm});
            skLineSegment(sketch, "E364", {"start": v(-30.13, -8.19) * mm, "end": v(-29.75, -7.28) * mm});
            skLineSegment(sketch, "E365", {"start": v(-29.75, -7.28) * mm, "end": v(-30.1, -6.63) * mm});
            skLineSegment(sketch, "E366", {"start": v(-30.1, -6.63) * mm, "end": v(-31.07, -5.92) * mm});
            skLineSegment(sketch, "E367", {"start": v(-31.07, -5.92) * mm, "end": v(-32.1, -5.92) * mm});
            skLineSegment(sketch, "E368", {"start": v(-32.1, -5.92) * mm, "end": v(-32.58, -5.56) * mm});
            skLineSegment(sketch, "E369", {"start": v(-32.58, -5.56) * mm, "end": v(-32.88, -4.91) * mm});
            skLineSegment(sketch, "E370", {"start": v(-32.88, -4.91) * mm, "end": v(-32.88, -4.63) * mm});
            skLineSegment(sketch, "E371", {"start": v(-32.88, -4.63) * mm, "end": v(-32.18, -4.26) * mm});
            skLineSegment(sketch, "E372", {"start": v(-32.18, -4.26) * mm, "end": v(-31, -4.41) * mm});
            skLineSegment(sketch, "E373", {"start": v(-31, -4.41) * mm, "end": v(-30.1, -4.7) * mm});
            skLineSegment(sketch, "E374", {"start": v(-30.1, -4.7) * mm, "end": v(-29.8, -4.54) * mm});
            skLineSegment(sketch, "E375", {"start": v(-29.8, -4.54) * mm, "end": v(-29.87, -4.3) * mm});
            skLineSegment(sketch, "E376", {"start": v(-6.53, 6.36) * mm, "end": v(-6.53, -19.08) * mm});
            skArc(sketch, "E377", {"start": v(-10.9, -23.24) * mm, "mid": v(-8.1, -21.8) * mm, "end": v(-6.53, -19.08) * mm});
            skLineSegment(sketch, "E378", {"start": v(-10.9, -23.24) * mm, "end": v(-36.05, -23.24) * mm});
            skArc(sketch, "E379", {"start": v(-40.27, -19.1) * mm, "mid": v(-38.72, -21.74) * mm, "end": v(-36.05, -23.24) * mm});
            skLineSegment(sketch, "E380", {"start": v(-40.27, -19.1) * mm, "end": v(-40.27, 6.4) * mm});
            skArc(sketch, "E381", {"start": v(-36.14, 10.5) * mm, "mid": v(-38.88, 9.12) * mm, "end": v(-40.27, 6.4) * mm});
            skLineSegment(sketch, "E382", {"start": v(-36.14, 10.5) * mm, "end": v(-10.74, 10.5) * mm});
            skArc(sketch, "E383", {"start": v(-6.53, 6.36) * mm, "mid": v(-8.06, 9.01) * mm, "end": v(-10.74, 10.5) * mm});
            skCircle(sketch, "E384", {"center": v(-23.52, 8.48) * mm, "radius": 1.56 * mm});
            skLineSegment(sketch, "E385", {"start": v(-23.4, -2.72) * mm, "end": v(-23.39, -5.52) * mm, "construction": true});
            skLineSegment(sketch, "E386", {"start": v(-23.39, -5.52) * mm, "end": v(-23.39, -23.24) * mm});
            skText(sketch, "E387", { "text": "David", "fontName": "OpenSans-Regular.ttf"});
            skPoint(sketch, "E388.middle", {"position": v(11.19, 36.2) * mm});
            skPoint(sketch, "E389.middle", {"position": v(11.31, 29.03) * mm});
            skLineSegment(sketch, "E390", {"start": v(4.83, 30.26) * mm, "end": v(5.02, 34.82) * mm});
            skLineSegment(sketch, "E391", {"start": v(5.02, 34.82) * mm, "end": v(5.21, 36.05) * mm});
            skLineSegment(sketch, "E392", {"start": v(5.21, 36.05) * mm, "end": v(6.54, 37.83) * mm});
            skLineSegment(sketch, "E393", {"start": v(6.54, 37.83) * mm, "end": v(8.54, 38.97) * mm});
            skLineSegment(sketch, "E394", {"start": v(8.54, 38.97) * mm, "end": v(10.39, 39.21) * mm});
            skLineSegment(sketch, "E395", {"start": v(10.39, 39.21) * mm, "end": v(12.15, 39.43) * mm});
            skLineSegment(sketch, "E396", {"start": v(12.15, 39.43) * mm, "end": v(13.2, 39.16) * mm});
            skLineSegment(sketch, "E397", {"start": v(13.2, 39.16) * mm, "end": v(14.9, 38.4) * mm});
            skLineSegment(sketch, "E398", {"start": v(14.9, 38.4) * mm, "end": v(15.66, 37.83) * mm});
            skLineSegment(sketch, "E399", {"start": v(15.66, 37.83) * mm, "end": v(16.75, 36.89) * mm});
            skLineSegment(sketch, "E400", {"start": v(16.75, 36.89) * mm, "end": v(17.13, 36.05) * mm});
            skLineSegment(sketch, "E401", {"start": v(17.13, 36.05) * mm, "end": v(17.56, 34.49) * mm});
            skLineSegment(sketch, "E402", {"start": v(17.56, 34.49) * mm, "end": v(17.56, 33) * mm});
            skLineSegment(sketch, "E403", {"start": v(17.56, 33) * mm, "end": v(17.65, 31.76) * mm});
            skLineSegment(sketch, "E404", {"start": v(17.65, 31.76) * mm, "end": v(17.65, 30.57) * mm});
            skLineSegment(sketch, "E405", {"start": v(17.65, 30.57) * mm, "end": v(17.65, 30.1) * mm});
            skLineSegment(sketch, "E406", {"start": v(17.65, 30.1) * mm, "end": v(18.5, 29.76) * mm});
            skLineSegment(sketch, "E407", {"start": v(18.5, 29.76) * mm, "end": v(19.79, 30.24) * mm});
            skLineSegment(sketch, "E408", {"start": v(19.79, 30.24) * mm, "end": v(20.31, 30.24) * mm});
            skLineSegment(sketch, "E409", {"start": v(20.31, 30.24) * mm, "end": v(20.7, 29.76) * mm});
            skLineSegment(sketch, "E410", {"start": v(20.7, 29.76) * mm, "end": v(20.7, 29.25) * mm});
            skLineSegment(sketch, "E411", {"start": v(20.7, 29.25) * mm, "end": v(20.35, 28.85) * mm});
            skLineSegment(sketch, "E412", {"start": v(20.35, 28.85) * mm, "end": v(19.76, 28.58) * mm});
            skLineSegment(sketch, "E413", {"start": v(19.76, 28.58) * mm, "end": v(19.36, 28.58) * mm});
            skLineSegment(sketch, "E414", {"start": v(19.36, 28.58) * mm, "end": v(18.67, 28.09) * mm});
            skLineSegment(sketch, "E415", {"start": v(18.67, 28.09) * mm, "end": v(17.92, 27.72) * mm});
            skLineSegment(sketch, "E416", {"start": v(17.92, 27.72) * mm, "end": v(17.92, 27.17) * mm});
            skLineSegment(sketch, "E417", {"start": v(17.92, 27.17) * mm, "end": v(17.92, 26.44) * mm});
            skLineSegment(sketch, "E418", {"start": v(17.92, 26.44) * mm, "end": v(18.21, 25.58) * mm});
            skLineSegment(sketch, "E419", {"start": v(18.21, 25.58) * mm, "end": v(19.13, 24.91) * mm});
            skLineSegment(sketch, "E420", {"start": v(19.13, 24.91) * mm, "end": v(20.24, 23.38) * mm});
            skLineSegment(sketch, "E421", {"start": v(20.24, 23.38) * mm, "end": v(21.1, 22.75) * mm});
            skLineSegment(sketch, "E422", {"start": v(21.1, 22.75) * mm, "end": v(21.84, 22.47) * mm});
            skLineSegment(sketch, "E423", {"start": v(21.84, 22.47) * mm, "end": v(22.76, 22.12) * mm});
            skLineSegment(sketch, "E424", {"start": v(22.76, 22.12) * mm, "end": v(23.3, 22.12) * mm});
            skLineSegment(sketch, "E425", {"start": v(23.3, 22.12) * mm, "end": v(23.03, 21.76) * mm});
            skLineSegment(sketch, "E426", {"start": v(23.03, 21.76) * mm, "end": v(22.91, 21.47) * mm});
            skLineSegment(sketch, "E427", {"start": v(22.91, 21.47) * mm, "end": v(22.45, 21.3) * mm});
            skLineSegment(sketch, "E428", {"start": v(22.45, 21.3) * mm, "end": v(21.17, 20.98) * mm});
            skLineSegment(sketch, "E429", {"start": v(21.17, 20.98) * mm, "end": v(20.39, 20.61) * mm});
            skLineSegment(sketch, "E430", {"start": v(20.39, 20.61) * mm, "end": v(19.95, 20.38) * mm});
            skLineSegment(sketch, "E431", {"start": v(19.95, 20.38) * mm, "end": v(19.76, 19.54) * mm});
            skLineSegment(sketch, "E432", {"start": v(19.76, 19.54) * mm, "end": v(19.13, 19.21) * mm});
            skLineSegment(sketch, "E433", {"start": v(19.13, 19.21) * mm, "end": v(17.27, 19.21) * mm});
            skLineSegment(sketch, "E434", {"start": v(17.27, 19.21) * mm, "end": v(16.33, 19.2) * mm});
            skLineSegment(sketch, "E435", {"start": v(16.33, 19.2) * mm, "end": v(15.13, 18.58) * mm});
            skLineSegment(sketch, "E436", {"start": v(15.13, 18.58) * mm, "end": v(14.73, 18.2) * mm});
            skLineSegment(sketch, "E437", {"start": v(14.73, 18.2) * mm, "end": v(13.81, 17.72) * mm});
            skLineSegment(sketch, "E438", {"start": v(13.81, 17.72) * mm, "end": v(13.24, 17.44) * mm});
            skLineSegment(sketch, "E439", {"start": v(13.24, 17.44) * mm, "end": v(12.05, 17.06) * mm});
            skLineSegment(sketch, "E440", {"start": v(12.05, 17.06) * mm, "end": v(11.64, 16.85) * mm});
            skLineSegment(sketch, "E441", {"start": v(11.64, 16.85) * mm, "end": v(10.44, 16.97) * mm});
            skLineSegment(sketch, "E442", {"start": v(10.44, 16.97) * mm, "end": v(9.54, 17.02) * mm});
            skLineSegment(sketch, "E443", {"start": v(9.54, 17.02) * mm, "end": v(8.64, 17.67) * mm});
            skLineSegment(sketch, "E444", {"start": v(8.64, 17.67) * mm, "end": v(7.6, 18.43) * mm});
            skLineSegment(sketch, "E445", {"start": v(7.6, 18.43) * mm, "end": v(7.02, 18.92) * mm});
            skLineSegment(sketch, "E446", {"start": v(7.02, 18.92) * mm, "end": v(6.1, 19.1) * mm});
            skLineSegment(sketch, "E447", {"start": v(6.1, 19.1) * mm, "end": v(4.93, 19.34) * mm});
            skLineSegment(sketch, "E448", {"start": v(4.93, 19.34) * mm, "end": v(4.08, 19.34) * mm});
            skLineSegment(sketch, "E449", {"start": v(4.08, 19.34) * mm, "end": v(3.7, 18.96) * mm});
            skLineSegment(sketch, "E450", {"start": v(3.7, 18.96) * mm, "end": v(2.65, 19.32) * mm});
            skLineSegment(sketch, "E451", {"start": v(2.65, 19.32) * mm, "end": v(2.65, 20.61) * mm});
            skLineSegment(sketch, "E452", {"start": v(2.65, 20.61) * mm, "end": v(1.47, 21.05) * mm});
            skLineSegment(sketch, "E453", {"start": v(1.47, 21.05) * mm, "end": v(0.06, 21.24) * mm});
            skLineSegment(sketch, "E454", {"start": v(0.06, 21.24) * mm, "end": v(-0.83, 21.9) * mm});
            skLineSegment(sketch, "E455", {"start": v(-0.83, 21.9) * mm, "end": v(-0.22, 22.21) * mm});
            skLineSegment(sketch, "E456", {"start": v(-0.22, 22.21) * mm, "end": v(0.87, 22.45) * mm});
            skLineSegment(sketch, "E457", {"start": v(0.87, 22.45) * mm, "end": v(1.63, 23.14) * mm});
            skLineSegment(sketch, "E458", {"start": v(1.63, 23.14) * mm, "end": v(3.77, 24.91) * mm});
            skLineSegment(sketch, "E459", {"start": v(3.77, 24.91) * mm, "end": v(4.45, 25.84) * mm});
            skLineSegment(sketch, "E460", {"start": v(4.45, 25.84) * mm, "end": v(4.57, 26.37) * mm});
            skLineSegment(sketch, "E461", {"start": v(4.57, 26.37) * mm, "end": v(4.95, 27.27) * mm});
            skLineSegment(sketch, "E462", {"start": v(4.95, 27.27) * mm, "end": v(4.61, 27.93) * mm});
            skLineSegment(sketch, "E463", {"start": v(4.61, 27.93) * mm, "end": v(3.64, 28.64) * mm});
            skLineSegment(sketch, "E464", {"start": v(3.64, 28.64) * mm, "end": v(2.6, 28.64) * mm});
            skLineSegment(sketch, "E465", {"start": v(2.6, 28.64) * mm, "end": v(2.12, 29) * mm});
            skLineSegment(sketch, "E466", {"start": v(2.12, 29) * mm, "end": v(1.82, 29.64) * mm});
            skLineSegment(sketch, "E467", {"start": v(1.82, 29.64) * mm, "end": v(1.82, 29.93) * mm});
            skLineSegment(sketch, "E468", {"start": v(1.82, 29.93) * mm, "end": v(2.52, 30.3) * mm});
            skLineSegment(sketch, "E469", {"start": v(2.52, 30.3) * mm, "end": v(3.7, 30.14) * mm});
            skLineSegment(sketch, "E470", {"start": v(3.7, 30.14) * mm, "end": v(4.61, 29.86) * mm});
            skLineSegment(sketch, "E471", {"start": v(4.61, 29.86) * mm, "end": v(4.91, 30.01) * mm});
            skLineSegment(sketch, "E472", {"start": v(4.91, 30.01) * mm, "end": v(4.83, 30.26) * mm});
            skLineSegment(sketch, "E473", {"start": v(28.17, 40.91) * mm, "end": v(28.17, 15.48) * mm});
            skArc(sketch, "E474", {"start": v(23.8, 11.32) * mm, "mid": v(26.6, 12.76) * mm, "end": v(28.17, 15.48) * mm});
            skLineSegment(sketch, "E475", {"start": v(23.8, 11.32) * mm, "end": v(-1.34, 11.32) * mm});
            skArc(sketch, "E476", {"start": v(-5.57, 15.46) * mm, "mid": v(-4.02, 12.82) * mm, "end": v(-1.34, 11.32) * mm});
            skLineSegment(sketch, "E477", {"start": v(-5.57, 15.46) * mm, "end": v(-5.57, 40.95) * mm});
            skArc(sketch, "E478", {"start": v(-1.44, 45.05) * mm, "mid": v(-4.17, 43.68) * mm, "end": v(-5.57, 40.95) * mm});
            skLineSegment(sketch, "E479", {"start": v(-1.44, 45.05) * mm, "end": v(23.96, 45.05) * mm});
            skArc(sketch, "E480", {"start": v(28.17, 40.91) * mm, "mid": v(26.64, 43.57) * mm, "end": v(23.96, 45.05) * mm});
            skCircle(sketch, "E481", {"center": v(11.19, 43.04) * mm, "radius": 1.56 * mm});
            skLineSegment(sketch, "E482", {"start": v(11.3, 31.84) * mm, "end": v(11.31, 29.03) * mm, "construction": true});
            skLineSegment(sketch, "E483", {"start": v(11.31, 29.03) * mm, "end": v(11.31, 11.32) * mm});
            skText(sketch, "E484", { "text": "Fritz", "fontName": "OpenSans-Regular.ttf"});
            skPoint(sketch, "E485.middle", {"position": v(11.19, 1.11) * mm});
            skPoint(sketch, "E486.middle", {"position": v(11.31, -6.04) * mm});
            skLineSegment(sketch, "E487", {"start": v(4.83, -4.81) * mm, "end": v(5.02, -0.26) * mm});
            skLineSegment(sketch, "E488", {"start": v(5.02, -0.26) * mm, "end": v(5.21, 0.98) * mm});
            skLineSegment(sketch, "E489", {"start": v(5.21, 0.98) * mm, "end": v(6.54, 2.76) * mm});
            skLineSegment(sketch, "E490", {"start": v(6.54, 2.76) * mm, "end": v(8.54, 3.9) * mm});
            skLineSegment(sketch, "E491", {"start": v(8.54, 3.9) * mm, "end": v(10.39, 4.14) * mm});
            skLineSegment(sketch, "E492", {"start": v(10.39, 4.14) * mm, "end": v(12.15, 4.35) * mm});
            skLineSegment(sketch, "E493", {"start": v(12.15, 4.35) * mm, "end": v(13.2, 4.09) * mm});
            skLineSegment(sketch, "E494", {"start": v(13.2, 4.09) * mm, "end": v(14.9, 3.33) * mm});
            skLineSegment(sketch, "E495", {"start": v(14.9, 3.33) * mm, "end": v(15.66, 2.76) * mm});
            skLineSegment(sketch, "E496", {"start": v(15.66, 2.76) * mm, "end": v(16.75, 1.8) * mm});
            skLineSegment(sketch, "E497", {"start": v(16.75, 1.8) * mm, "end": v(17.13, 0.98) * mm});
            skLineSegment(sketch, "E498", {"start": v(17.13, 0.98) * mm, "end": v(17.56, -0.59) * mm});
            skLineSegment(sketch, "E499", {"start": v(17.56, -0.59) * mm, "end": v(17.56, -2.08) * mm});
            skLineSegment(sketch, "E500", {"start": v(17.56, -2.08) * mm, "end": v(17.65, -3.32) * mm});
            skLineSegment(sketch, "E501", {"start": v(17.65, -3.32) * mm, "end": v(17.65, -4.5) * mm});
            skLineSegment(sketch, "E502", {"start": v(17.65, -4.5) * mm, "end": v(17.65, -4.98) * mm});
            skLineSegment(sketch, "E503", {"start": v(17.65, -4.98) * mm, "end": v(18.5, -5.31) * mm});
            skLineSegment(sketch, "E504", {"start": v(18.5, -5.31) * mm, "end": v(19.79, -4.84) * mm});
            skLineSegment(sketch, "E505", {"start": v(19.79, -4.84) * mm, "end": v(20.31, -4.84) * mm});
            skLineSegment(sketch, "E506", {"start": v(20.31, -4.84) * mm, "end": v(20.7, -5.31) * mm});
            skLineSegment(sketch, "E507", {"start": v(20.7, -5.31) * mm, "end": v(20.7, -5.82) * mm});
            skLineSegment(sketch, "E508", {"start": v(20.7, -5.82) * mm, "end": v(20.35, -6.23) * mm});
            skLineSegment(sketch, "E509", {"start": v(20.35, -6.23) * mm, "end": v(19.76, -6.5) * mm});
            skLineSegment(sketch, "E510", {"start": v(19.76, -6.5) * mm, "end": v(19.36, -6.5) * mm});
            skLineSegment(sketch, "E511", {"start": v(19.36, -6.5) * mm, "end": v(18.67, -7) * mm});
            skLineSegment(sketch, "E512", {"start": v(18.67, -7) * mm, "end": v(17.92, -7.35) * mm});
            skLineSegment(sketch, "E513", {"start": v(17.92, -7.35) * mm, "end": v(17.92, -7.9) * mm});
            skLineSegment(sketch, "E514", {"start": v(17.92, -7.9) * mm, "end": v(17.92, -8.63) * mm});
            skLineSegment(sketch, "E515", {"start": v(17.92, -8.63) * mm, "end": v(18.21, -9.5) * mm});
            skLineSegment(sketch, "E516", {"start": v(18.21, -9.5) * mm, "end": v(19.13, -10.16) * mm});
            skLineSegment(sketch, "E517", {"start": v(19.13, -10.16) * mm, "end": v(20.24, -11.7) * mm});
            skLineSegment(sketch, "E518", {"start": v(20.24, -11.7) * mm, "end": v(21.1, -12.32) * mm});
            skLineSegment(sketch, "E519", {"start": v(21.1, -12.32) * mm, "end": v(21.84, -12.61) * mm});
            skLineSegment(sketch, "E520", {"start": v(21.84, -12.61) * mm, "end": v(22.76, -12.95) * mm});
            skLineSegment(sketch, "E521", {"start": v(22.76, -12.95) * mm, "end": v(23.3, -12.95) * mm});
            skLineSegment(sketch, "E522", {"start": v(23.3, -12.95) * mm, "end": v(23.03, -13.32) * mm});
            skLineSegment(sketch, "E523", {"start": v(23.03, -13.32) * mm, "end": v(22.91, -13.6) * mm});
            skLineSegment(sketch, "E524", {"start": v(22.91, -13.6) * mm, "end": v(22.45, -13.78) * mm});
            skLineSegment(sketch, "E525", {"start": v(22.45, -13.78) * mm, "end": v(21.17, -14.1) * mm});
            skLineSegment(sketch, "E526", {"start": v(21.17, -14.1) * mm, "end": v(20.39, -14.46) * mm});
            skLineSegment(sketch, "E527", {"start": v(20.39, -14.46) * mm, "end": v(19.95, -14.7) * mm});
            skLineSegment(sketch, "E528", {"start": v(19.95, -14.7) * mm, "end": v(19.76, -15.53) * mm});
            skLineSegment(sketch, "E529", {"start": v(19.76, -15.53) * mm, "end": v(19.13, -15.86) * mm});
            skLineSegment(sketch, "E530", {"start": v(19.13, -15.86) * mm, "end": v(17.27, -15.86) * mm});
            skLineSegment(sketch, "E531", {"start": v(17.27, -15.86) * mm, "end": v(16.33, -15.88) * mm});
            skLineSegment(sketch, "E532", {"start": v(16.33, -15.88) * mm, "end": v(15.13, -16.5) * mm});
            skLineSegment(sketch, "E533", {"start": v(15.13, -16.5) * mm, "end": v(14.73, -16.87) * mm});
            skLineSegment(sketch, "E534", {"start": v(14.73, -16.87) * mm, "end": v(13.81, -17.36) * mm});
            skLineSegment(sketch, "E535", {"start": v(13.81, -17.36) * mm, "end": v(13.24, -17.63) * mm});
            skLineSegment(sketch, "E536", {"start": v(13.24, -17.63) * mm, "end": v(12.05, -18.01) * mm});
            skLineSegment(sketch, "E537", {"start": v(12.05, -18.01) * mm, "end": v(11.64, -18.23) * mm});
            skLineSegment(sketch, "E538", {"start": v(11.64, -18.23) * mm, "end": v(10.44, -18.1) * mm});
            skLineSegment(sketch, "E539", {"start": v(10.44, -18.1) * mm, "end": v(9.54, -18.06) * mm});
            skLineSegment(sketch, "E540", {"start": v(9.54, -18.06) * mm, "end": v(8.64, -17.4) * mm});
            skLineSegment(sketch, "E541", {"start": v(8.64, -17.4) * mm, "end": v(7.6, -16.64) * mm});
            skLineSegment(sketch, "E542", {"start": v(7.6, -16.64) * mm, "end": v(7.02, -16.16) * mm});
            skLineSegment(sketch, "E543", {"start": v(7.02, -16.16) * mm, "end": v(6.1, -15.97) * mm});
            skLineSegment(sketch, "E544", {"start": v(6.1, -15.97) * mm, "end": v(4.93, -15.73) * mm});
            skLineSegment(sketch, "E545", {"start": v(4.93, -15.73) * mm, "end": v(4.08, -15.73) * mm});
            skLineSegment(sketch, "E546", {"start": v(4.08, -15.73) * mm, "end": v(3.7, -16.11) * mm});
            skLineSegment(sketch, "E547", {"start": v(3.7, -16.11) * mm, "end": v(2.65, -15.76) * mm});
            skLineSegment(sketch, "E548", {"start": v(2.65, -15.76) * mm, "end": v(2.65, -14.46) * mm});
            skLineSegment(sketch, "E549", {"start": v(2.65, -14.46) * mm, "end": v(1.47, -14.02) * mm});
            skLineSegment(sketch, "E550", {"start": v(1.47, -14.02) * mm, "end": v(0.06, -13.84) * mm});
            skLineSegment(sketch, "E551", {"start": v(0.06, -13.84) * mm, "end": v(-0.83, -13.18) * mm});
            skLineSegment(sketch, "E552", {"start": v(-0.83, -13.18) * mm, "end": v(-0.22, -12.86) * mm});
            skLineSegment(sketch, "E553", {"start": v(-0.22, -12.86) * mm, "end": v(0.87, -12.62) * mm});
            skLineSegment(sketch, "E554", {"start": v(0.87, -12.62) * mm, "end": v(1.63, -11.94) * mm});
            skLineSegment(sketch, "E555", {"start": v(1.63, -11.94) * mm, "end": v(3.77, -10.16) * mm});
            skLineSegment(sketch, "E556", {"start": v(3.77, -10.16) * mm, "end": v(4.45, -9.23) * mm});
            skLineSegment(sketch, "E557", {"start": v(4.45, -9.23) * mm, "end": v(4.57, -8.7) * mm});
            skLineSegment(sketch, "E558", {"start": v(4.57, -8.7) * mm, "end": v(4.95, -7.8) * mm});
            skLineSegment(sketch, "E559", {"start": v(4.95, -7.8) * mm, "end": v(4.61, -7.15) * mm});
            skLineSegment(sketch, "E560", {"start": v(4.61, -7.15) * mm, "end": v(3.64, -6.44) * mm});
            skLineSegment(sketch, "E561", {"start": v(3.64, -6.44) * mm, "end": v(2.6, -6.44) * mm});
            skLineSegment(sketch, "E562", {"start": v(2.6, -6.44) * mm, "end": v(2.12, -6.08) * mm});
            skLineSegment(sketch, "E563", {"start": v(2.12, -6.08) * mm, "end": v(1.82, -5.43) * mm});
            skLineSegment(sketch, "E564", {"start": v(1.82, -5.43) * mm, "end": v(1.82, -5.15) * mm});
            skLineSegment(sketch, "E565", {"start": v(1.82, -5.15) * mm, "end": v(2.52, -4.78) * mm});
            skLineSegment(sketch, "E566", {"start": v(2.52, -4.78) * mm, "end": v(3.7, -4.93) * mm});
            skLineSegment(sketch, "E567", {"start": v(3.7, -4.93) * mm, "end": v(4.61, -5.22) * mm});
            skLineSegment(sketch, "E568", {"start": v(4.61, -5.22) * mm, "end": v(4.91, -5.06) * mm});
            skLineSegment(sketch, "E569", {"start": v(4.91, -5.06) * mm, "end": v(4.83, -4.81) * mm});
            skLineSegment(sketch, "E570", {"start": v(28.17, 5.84) * mm, "end": v(28.17, -19.6) * mm});
            skArc(sketch, "E571", {"start": v(23.8, -23.76) * mm, "mid": v(26.6, -22.32) * mm, "end": v(28.17, -19.6) * mm});
            skLineSegment(sketch, "E572", {"start": v(23.8, -23.76) * mm, "end": v(-1.34, -23.76) * mm});
            skArc(sketch, "E573", {"start": v(-5.57, -19.62) * mm, "mid": v(-4.02, -22.26) * mm, "end": v(-1.34, -23.76) * mm});
            skLineSegment(sketch, "E574", {"start": v(-5.57, -19.62) * mm, "end": v(-5.57, 5.87) * mm});
            skArc(sketch, "E575", {"start": v(-1.44, 9.98) * mm, "mid": v(-4.17, 8.6) * mm, "end": v(-5.57, 5.87) * mm});
            skLineSegment(sketch, "E576", {"start": v(-1.44, 9.98) * mm, "end": v(23.96, 9.98) * mm});
            skArc(sketch, "E577", {"start": v(28.17, 5.84) * mm, "mid": v(26.64, 8.5) * mm, "end": v(23.96, 9.98) * mm});
            skCircle(sketch, "E578", {"center": v(11.19, 7.96) * mm, "radius": 1.56 * mm});
            skLineSegment(sketch, "E579", {"start": v(11.3, -3.24) * mm, "end": v(11.31, -6.04) * mm, "construction": true});
            skLineSegment(sketch, "E580", {"start": v(11.31, -6.04) * mm, "end": v(11.31, -23.76) * mm});
            skText(sketch, "E581", { "text": "Tadas", "fontName": "OpenSans-Regular.ttf"});
            skPoint(sketch, "E582.middle", {"position": v(45.99, 36.25) * mm});
            skPoint(sketch, "E583.middle", {"position": v(46.12, 29.1) * mm});
            skLineSegment(sketch, "E584", {"start": v(39.64, 30.32) * mm, "end": v(39.83, 34.88) * mm});
            skLineSegment(sketch, "E585", {"start": v(39.83, 34.88) * mm, "end": v(40.02, 36.12) * mm});
            skLineSegment(sketch, "E586", {"start": v(40.02, 36.12) * mm, "end": v(41.34, 37.9) * mm});
            skLineSegment(sketch, "E587", {"start": v(41.34, 37.9) * mm, "end": v(43.34, 39.03) * mm});
            skLineSegment(sketch, "E588", {"start": v(43.34, 39.03) * mm, "end": v(45.2, 39.27) * mm});
            skLineSegment(sketch, "E589", {"start": v(45.2, 39.27) * mm, "end": v(46.95, 39.49) * mm});
            skLineSegment(sketch, "E590", {"start": v(46.95, 39.49) * mm, "end": v(48, 39.22) * mm});
            skLineSegment(sketch, "E591", {"start": v(48, 39.22) * mm, "end": v(49.7, 38.47) * mm});
            skLineSegment(sketch, "E592", {"start": v(49.7, 38.47) * mm, "end": v(50.46, 37.9) * mm});
            skLineSegment(sketch, "E593", {"start": v(50.46, 37.9) * mm, "end": v(51.55, 36.95) * mm});
            skLineSegment(sketch, "E594", {"start": v(51.55, 36.95) * mm, "end": v(51.93, 36.12) * mm});
            skLineSegment(sketch, "E595", {"start": v(51.93, 36.12) * mm, "end": v(52.36, 34.55) * mm});
            skLineSegment(sketch, "E596", {"start": v(52.36, 34.55) * mm, "end": v(52.36, 33.05) * mm});
            skLineSegment(sketch, "E597", {"start": v(52.36, 33.05) * mm, "end": v(52.45, 31.82) * mm});
            skLineSegment(sketch, "E598", {"start": v(52.45, 31.82) * mm, "end": v(52.45, 30.63) * mm});
            skLineSegment(sketch, "E599", {"start": v(52.45, 30.63) * mm, "end": v(52.45, 30.16) * mm});
            skLineSegment(sketch, "E600", {"start": v(52.45, 30.16) * mm, "end": v(53.3, 29.82) * mm});
            skLineSegment(sketch, "E601", {"start": v(53.3, 29.82) * mm, "end": v(54.6, 30.3) * mm});
            skLineSegment(sketch, "E602", {"start": v(54.6, 30.3) * mm, "end": v(55.11, 30.3) * mm});
            skLineSegment(sketch, "E603", {"start": v(55.11, 30.3) * mm, "end": v(55.5, 29.82) * mm});
            skLineSegment(sketch, "E604", {"start": v(55.5, 29.82) * mm, "end": v(55.5, 29.31) * mm});
            skLineSegment(sketch, "E605", {"start": v(55.5, 29.31) * mm, "end": v(55.15, 28.91) * mm});
            skLineSegment(sketch, "E606", {"start": v(55.15, 28.91) * mm, "end": v(54.56, 28.64) * mm});
            skLineSegment(sketch, "E607", {"start": v(54.56, 28.64) * mm, "end": v(54.16, 28.64) * mm});
            skLineSegment(sketch, "E608", {"start": v(54.16, 28.64) * mm, "end": v(53.47, 28.15) * mm});
            skLineSegment(sketch, "E609", {"start": v(53.47, 28.15) * mm, "end": v(52.73, 27.78) * mm});
            skLineSegment(sketch, "E610", {"start": v(52.73, 27.78) * mm, "end": v(52.73, 27.23) * mm});
            skLineSegment(sketch, "E611", {"start": v(52.73, 27.23) * mm, "end": v(52.73, 26.5) * mm});
            skLineSegment(sketch, "E612", {"start": v(52.73, 26.5) * mm, "end": v(53.01, 25.64) * mm});
            skLineSegment(sketch, "E613", {"start": v(53.01, 25.64) * mm, "end": v(53.93, 24.97) * mm});
            skLineSegment(sketch, "E614", {"start": v(53.93, 24.97) * mm, "end": v(55.04, 23.44) * mm});
            skLineSegment(sketch, "E615", {"start": v(55.04, 23.44) * mm, "end": v(55.9, 22.81) * mm});
            skLineSegment(sketch, "E616", {"start": v(55.9, 22.81) * mm, "end": v(56.64, 22.53) * mm});
            skLineSegment(sketch, "E617", {"start": v(56.64, 22.53) * mm, "end": v(57.56, 22.18) * mm});
            skLineSegment(sketch, "E618", {"start": v(57.56, 22.18) * mm, "end": v(58.1, 22.18) * mm});
            skLineSegment(sketch, "E619", {"start": v(58.1, 22.18) * mm, "end": v(57.83, 21.82) * mm});
            skLineSegment(sketch, "E620", {"start": v(57.83, 21.82) * mm, "end": v(57.71, 21.53) * mm});
            skLineSegment(sketch, "E621", {"start": v(57.71, 21.53) * mm, "end": v(57.26, 21.36) * mm});
            skLineSegment(sketch, "E622", {"start": v(57.26, 21.36) * mm, "end": v(55.97, 21.04) * mm});
            skLineSegment(sketch, "E623", {"start": v(55.97, 21.04) * mm, "end": v(55.2, 20.67) * mm});
            skLineSegment(sketch, "E624", {"start": v(55.2, 20.67) * mm, "end": v(54.75, 20.44) * mm});
            skLineSegment(sketch, "E625", {"start": v(54.75, 20.44) * mm, "end": v(54.56, 19.6) * mm});
            skLineSegment(sketch, "E626", {"start": v(54.56, 19.6) * mm, "end": v(53.93, 19.27) * mm});
            skLineSegment(sketch, "E627", {"start": v(53.93, 19.27) * mm, "end": v(52.08, 19.27) * mm});
            skLineSegment(sketch, "E628", {"start": v(52.08, 19.27) * mm, "end": v(51.13, 19.26) * mm});
            skLineSegment(sketch, "E629", {"start": v(51.13, 19.26) * mm, "end": v(49.93, 18.64) * mm});
            skLineSegment(sketch, "E630", {"start": v(49.93, 18.64) * mm, "end": v(49.54, 18.26) * mm});
            skLineSegment(sketch, "E631", {"start": v(49.54, 18.26) * mm, "end": v(48.61, 17.78) * mm});
            skLineSegment(sketch, "E632", {"start": v(48.61, 17.78) * mm, "end": v(48.04, 17.5) * mm});
            skLineSegment(sketch, "E633", {"start": v(48.04, 17.5) * mm, "end": v(46.85, 17.12) * mm});
            skLineSegment(sketch, "E634", {"start": v(46.85, 17.12) * mm, "end": v(46.44, 16.9) * mm});
            skLineSegment(sketch, "E635", {"start": v(46.44, 16.9) * mm, "end": v(45.24, 17.03) * mm});
            skLineSegment(sketch, "E636", {"start": v(45.24, 17.03) * mm, "end": v(44.34, 17.08) * mm});
            skLineSegment(sketch, "E637", {"start": v(44.34, 17.08) * mm, "end": v(43.44, 17.73) * mm});
            skLineSegment(sketch, "E638", {"start": v(43.44, 17.73) * mm, "end": v(42.4, 18.5) * mm});
            skLineSegment(sketch, "E639", {"start": v(42.4, 18.5) * mm, "end": v(41.82, 18.98) * mm});
            skLineSegment(sketch, "E640", {"start": v(41.82, 18.98) * mm, "end": v(40.9, 19.17) * mm});
            skLineSegment(sketch, "E641", {"start": v(40.9, 19.17) * mm, "end": v(39.73, 19.4) * mm});
            skLineSegment(sketch, "E642", {"start": v(39.73, 19.4) * mm, "end": v(38.88, 19.4) * mm});
            skLineSegment(sketch, "E643", {"start": v(38.88, 19.4) * mm, "end": v(38.5, 19.02) * mm});
            skLineSegment(sketch, "E644", {"start": v(38.5, 19.02) * mm, "end": v(37.45, 19.38) * mm});
            skLineSegment(sketch, "E645", {"start": v(37.45, 19.38) * mm, "end": v(37.45, 20.67) * mm});
            skLineSegment(sketch, "E646", {"start": v(37.45, 20.67) * mm, "end": v(36.27, 21.11) * mm});
            skLineSegment(sketch, "E647", {"start": v(36.27, 21.11) * mm, "end": v(34.87, 21.3) * mm});
            skLineSegment(sketch, "E648", {"start": v(34.87, 21.3) * mm, "end": v(33.97, 21.95) * mm});
            skLineSegment(sketch, "E649", {"start": v(33.97, 21.95) * mm, "end": v(34.58, 22.27) * mm});
            skLineSegment(sketch, "E650", {"start": v(34.58, 22.27) * mm, "end": v(35.67, 22.51) * mm});
            skLineSegment(sketch, "E651", {"start": v(35.67, 22.51) * mm, "end": v(36.43, 23.2) * mm});
            skLineSegment(sketch, "E652", {"start": v(36.43, 23.2) * mm, "end": v(38.57, 24.97) * mm});
            skLineSegment(sketch, "E653", {"start": v(38.57, 24.97) * mm, "end": v(39.25, 25.9) * mm});
            skLineSegment(sketch, "E654", {"start": v(39.25, 25.9) * mm, "end": v(39.38, 26.43) * mm});
            skLineSegment(sketch, "E655", {"start": v(39.38, 26.43) * mm, "end": v(39.76, 27.33) * mm});
            skLineSegment(sketch, "E656", {"start": v(39.76, 27.33) * mm, "end": v(39.41, 27.99) * mm});
            skLineSegment(sketch, "E657", {"start": v(39.41, 27.99) * mm, "end": v(38.44, 28.7) * mm});
            skLineSegment(sketch, "E658", {"start": v(38.44, 28.7) * mm, "end": v(37.4, 28.7) * mm});
            skLineSegment(sketch, "E659", {"start": v(37.4, 28.7) * mm, "end": v(36.92, 29.05) * mm});
            skLineSegment(sketch, "E660", {"start": v(36.92, 29.05) * mm, "end": v(36.62, 29.7) * mm});
            skLineSegment(sketch, "E661", {"start": v(36.62, 29.7) * mm, "end": v(36.62, 30) * mm});
            skLineSegment(sketch, "E662", {"start": v(36.62, 30) * mm, "end": v(37.32, 30.35) * mm});
            skLineSegment(sketch, "E663", {"start": v(37.32, 30.35) * mm, "end": v(38.5, 30.2) * mm});
            skLineSegment(sketch, "E664", {"start": v(38.5, 30.2) * mm, "end": v(39.41, 29.92) * mm});
            skLineSegment(sketch, "E665", {"start": v(39.41, 29.92) * mm, "end": v(39.71, 30.08) * mm});
            skLineSegment(sketch, "E666", {"start": v(39.71, 30.08) * mm, "end": v(39.64, 30.32) * mm});
            skLineSegment(sketch, "E667", {"start": v(62.97, 40.98) * mm, "end": v(62.97, 15.54) * mm});
            skArc(sketch, "E668", {"start": v(58.6, 11.38) * mm, "mid": v(61.4, 12.82) * mm, "end": v(62.97, 15.54) * mm});
            skLineSegment(sketch, "E669", {"start": v(58.6, 11.38) * mm, "end": v(33.46, 11.38) * mm});
            skArc(sketch, "E670", {"start": v(29.23, 15.52) * mm, "mid": v(30.78, 12.88) * mm, "end": v(33.46, 11.38) * mm});
            skLineSegment(sketch, "E671", {"start": v(29.23, 15.52) * mm, "end": v(29.23, 41) * mm});
            skArc(sketch, "E672", {"start": v(33.37, 45.11) * mm, "mid": v(30.63, 43.74) * mm, "end": v(29.23, 41) * mm});
            skLineSegment(sketch, "E673", {"start": v(33.37, 45.11) * mm, "end": v(58.77, 45.11) * mm});
            skArc(sketch, "E674", {"start": v(62.97, 40.98) * mm, "mid": v(61.44, 43.63) * mm, "end": v(58.77, 45.11) * mm});
            skCircle(sketch, "E675", {"center": v(45.99, 43.1) * mm, "radius": 1.56 * mm});
            skLineSegment(sketch, "E676", {"start": v(46.1, 31.9) * mm, "end": v(46.12, 29.1) * mm, "construction": true});
            skLineSegment(sketch, "E677", {"start": v(46.12, 29.1) * mm, "end": v(46.12, 11.38) * mm});
            skText(sketch, "E678", { "text": "Nirthieca", "fontName": "OpenSans-Regular.ttf"});
            skPoint(sketch, "E679.middle", {"position": v(45.99, 1.3) * mm});
            skPoint(sketch, "E680.middle", {"position": v(46.12, -5.86) * mm});
            skLineSegment(sketch, "E681", {"start": v(39.64, -4.63) * mm, "end": v(39.83, -0.07) * mm});
            skLineSegment(sketch, "E682", {"start": v(39.83, -0.07) * mm, "end": v(40.02, 1.17) * mm});
            skLineSegment(sketch, "E683", {"start": v(40.02, 1.17) * mm, "end": v(41.34, 2.95) * mm});
            skLineSegment(sketch, "E684", {"start": v(41.34, 2.95) * mm, "end": v(43.34, 4.09) * mm});
            skLineSegment(sketch, "E685", {"start": v(43.34, 4.09) * mm, "end": v(45.2, 4.32) * mm});
            skLineSegment(sketch, "E686", {"start": v(45.2, 4.32) * mm, "end": v(46.95, 4.54) * mm});
            skLineSegment(sketch, "E687", {"start": v(46.95, 4.54) * mm, "end": v(48, 4.28) * mm});
            skLineSegment(sketch, "E688", {"start": v(48, 4.28) * mm, "end": v(49.7, 3.52) * mm});
            skLineSegment(sketch, "E689", {"start": v(49.7, 3.52) * mm, "end": v(50.46, 2.95) * mm});
            skLineSegment(sketch, "E690", {"start": v(50.46, 2.95) * mm, "end": v(51.55, 2) * mm});
            skLineSegment(sketch, "E691", {"start": v(51.55, 2) * mm, "end": v(51.93, 1.17) * mm});
            skLineSegment(sketch, "E692", {"start": v(51.93, 1.17) * mm, "end": v(52.36, -0.4) * mm});
            skLineSegment(sketch, "E693", {"start": v(52.36, -0.4) * mm, "end": v(52.36, -1.9) * mm});
            skLineSegment(sketch, "E694", {"start": v(52.36, -1.9) * mm, "end": v(52.45, -3.13) * mm});
            skLineSegment(sketch, "E695", {"start": v(52.45, -3.13) * mm, "end": v(52.45, -4.32) * mm});
            skLineSegment(sketch, "E696", {"start": v(52.45, -4.32) * mm, "end": v(52.45, -4.8) * mm});
            skLineSegment(sketch, "E697", {"start": v(52.45, -4.8) * mm, "end": v(53.3, -5.13) * mm});
            skLineSegment(sketch, "E698", {"start": v(53.3, -5.13) * mm, "end": v(54.6, -4.65) * mm});
            skLineSegment(sketch, "E699", {"start": v(54.6, -4.65) * mm, "end": v(55.11, -4.65) * mm});
            skLineSegment(sketch, "E700", {"start": v(55.11, -4.65) * mm, "end": v(55.5, -5.13) * mm});
            skLineSegment(sketch, "E701", {"start": v(55.5, -5.13) * mm, "end": v(55.5, -5.64) * mm});
            skLineSegment(sketch, "E702", {"start": v(55.5, -5.64) * mm, "end": v(55.15, -6.04) * mm});
            skLineSegment(sketch, "E703", {"start": v(55.15, -6.04) * mm, "end": v(54.56, -6.3) * mm});
            skLineSegment(sketch, "E704", {"start": v(54.56, -6.3) * mm, "end": v(54.16, -6.3) * mm});
            skLineSegment(sketch, "E705", {"start": v(54.16, -6.3) * mm, "end": v(53.47, -6.8) * mm});
            skLineSegment(sketch, "E706", {"start": v(53.47, -6.8) * mm, "end": v(52.73, -7.17) * mm});
            skLineSegment(sketch, "E707", {"start": v(52.73, -7.17) * mm, "end": v(52.73, -7.72) * mm});
            skLineSegment(sketch, "E708", {"start": v(52.73, -7.72) * mm, "end": v(52.73, -8.45) * mm});
            skLineSegment(sketch, "E709", {"start": v(52.73, -8.45) * mm, "end": v(53.01, -9.3) * mm});
            skLineSegment(sketch, "E710", {"start": v(53.01, -9.3) * mm, "end": v(53.93, -9.98) * mm});
            skLineSegment(sketch, "E711", {"start": v(53.93, -9.98) * mm, "end": v(55.04, -11.5) * mm});
            skLineSegment(sketch, "E712", {"start": v(55.04, -11.5) * mm, "end": v(55.9, -12.14) * mm});
            skLineSegment(sketch, "E713", {"start": v(55.9, -12.14) * mm, "end": v(56.64, -12.42) * mm});
            skLineSegment(sketch, "E714", {"start": v(56.64, -12.42) * mm, "end": v(57.56, -12.77) * mm});
            skLineSegment(sketch, "E715", {"start": v(57.56, -12.77) * mm, "end": v(58.1, -12.77) * mm});
            skLineSegment(sketch, "E716", {"start": v(58.1, -12.77) * mm, "end": v(57.83, -13.13) * mm});
            skLineSegment(sketch, "E717", {"start": v(57.83, -13.13) * mm, "end": v(57.71, -13.42) * mm});
            skLineSegment(sketch, "E718", {"start": v(57.71, -13.42) * mm, "end": v(57.26, -13.59) * mm});
            skLineSegment(sketch, "E719", {"start": v(57.26, -13.59) * mm, "end": v(55.97, -13.91) * mm});
            skLineSegment(sketch, "E720", {"start": v(55.97, -13.91) * mm, "end": v(55.2, -14.28) * mm});
            skLineSegment(sketch, "E721", {"start": v(55.2, -14.28) * mm, "end": v(54.75, -14.5) * mm});
            skLineSegment(sketch, "E722", {"start": v(54.75, -14.5) * mm, "end": v(54.56, -15.35) * mm});
            skLineSegment(sketch, "E723", {"start": v(54.56, -15.35) * mm, "end": v(53.93, -15.68) * mm});
            skLineSegment(sketch, "E724", {"start": v(53.93, -15.68) * mm, "end": v(52.08, -15.68) * mm});
            skLineSegment(sketch, "E725", {"start": v(52.08, -15.68) * mm, "end": v(51.13, -15.69) * mm});
            skLineSegment(sketch, "E726", {"start": v(51.13, -15.69) * mm, "end": v(49.93, -16.31) * mm});
            skLineSegment(sketch, "E727", {"start": v(49.93, -16.31) * mm, "end": v(49.54, -16.69) * mm});
            skLineSegment(sketch, "E728", {"start": v(49.54, -16.69) * mm, "end": v(48.61, -17.17) * mm});
            skLineSegment(sketch, "E729", {"start": v(48.61, -17.17) * mm, "end": v(48.04, -17.45) * mm});
            skLineSegment(sketch, "E730", {"start": v(48.04, -17.45) * mm, "end": v(46.85, -17.83) * mm});
            skLineSegment(sketch, "E731", {"start": v(46.85, -17.83) * mm, "end": v(46.44, -18.04) * mm});
            skLineSegment(sketch, "E732", {"start": v(46.44, -18.04) * mm, "end": v(45.24, -17.92) * mm});
            skLineSegment(sketch, "E733", {"start": v(45.24, -17.92) * mm, "end": v(44.34, -17.87) * mm});
            skLineSegment(sketch, "E734", {"start": v(44.34, -17.87) * mm, "end": v(43.44, -17.22) * mm});
            skLineSegment(sketch, "E735", {"start": v(43.44, -17.22) * mm, "end": v(42.4, -16.46) * mm});
            skLineSegment(sketch, "E736", {"start": v(42.4, -16.46) * mm, "end": v(41.82, -15.97) * mm});
            skLineSegment(sketch, "E737", {"start": v(41.82, -15.97) * mm, "end": v(40.9, -15.78) * mm});
            skLineSegment(sketch, "E738", {"start": v(40.9, -15.78) * mm, "end": v(39.73, -15.55) * mm});
            skLineSegment(sketch, "E739", {"start": v(39.73, -15.55) * mm, "end": v(38.88, -15.55) * mm});
            skLineSegment(sketch, "E740", {"start": v(38.88, -15.55) * mm, "end": v(38.5, -15.93) * mm});
            skLineSegment(sketch, "E741", {"start": v(38.5, -15.93) * mm, "end": v(37.45, -15.57) * mm});
            skLineSegment(sketch, "E742", {"start": v(37.45, -15.57) * mm, "end": v(37.45, -14.28) * mm});
            skLineSegment(sketch, "E743", {"start": v(37.45, -14.28) * mm, "end": v(36.27, -13.84) * mm});
            skLineSegment(sketch, "E744", {"start": v(36.27, -13.84) * mm, "end": v(34.87, -13.65) * mm});
            skLineSegment(sketch, "E745", {"start": v(34.87, -13.65) * mm, "end": v(33.97, -13) * mm});
            skLineSegment(sketch, "E746", {"start": v(33.97, -13) * mm, "end": v(34.58, -12.68) * mm});
            skLineSegment(sketch, "E747", {"start": v(34.58, -12.68) * mm, "end": v(35.67, -12.44) * mm});
            skLineSegment(sketch, "E748", {"start": v(35.67, -12.44) * mm, "end": v(36.43, -11.75) * mm});
            skLineSegment(sketch, "E749", {"start": v(36.43, -11.75) * mm, "end": v(38.57, -9.98) * mm});
            skLineSegment(sketch, "E750", {"start": v(38.57, -9.98) * mm, "end": v(39.25, -9.05) * mm});
            skLineSegment(sketch, "E751", {"start": v(39.25, -9.05) * mm, "end": v(39.38, -8.52) * mm});
            skLineSegment(sketch, "E752", {"start": v(39.38, -8.52) * mm, "end": v(39.76, -7.62) * mm});
            skLineSegment(sketch, "E753", {"start": v(39.76, -7.62) * mm, "end": v(39.41, -6.96) * mm});
            skLineSegment(sketch, "E754", {"start": v(39.41, -6.96) * mm, "end": v(38.44, -6.25) * mm});
            skLineSegment(sketch, "E755", {"start": v(38.44, -6.25) * mm, "end": v(37.4, -6.25) * mm});
            skLineSegment(sketch, "E756", {"start": v(37.4, -6.25) * mm, "end": v(36.92, -5.9) * mm});
            skLineSegment(sketch, "E757", {"start": v(36.92, -5.9) * mm, "end": v(36.62, -5.24) * mm});
            skLineSegment(sketch, "E758", {"start": v(36.62, -5.24) * mm, "end": v(36.62, -4.96) * mm});
            skLineSegment(sketch, "E759", {"start": v(36.62, -4.96) * mm, "end": v(37.32, -4.6) * mm});
            skLineSegment(sketch, "E760", {"start": v(37.32, -4.6) * mm, "end": v(38.5, -4.75) * mm});
            skLineSegment(sketch, "E761", {"start": v(38.5, -4.75) * mm, "end": v(39.41, -5.03) * mm});
            skLineSegment(sketch, "E762", {"start": v(39.41, -5.03) * mm, "end": v(39.71, -4.87) * mm});
            skLineSegment(sketch, "E763", {"start": v(39.71, -4.87) * mm, "end": v(39.64, -4.63) * mm});
            skLineSegment(sketch, "E764", {"start": v(62.97, 6.03) * mm, "end": v(62.97, -19.4) * mm});
            skArc(sketch, "E765", {"start": v(58.6, -23.57) * mm, "mid": v(61.4, -22.13) * mm, "end": v(62.97, -19.4) * mm});
            skLineSegment(sketch, "E766", {"start": v(58.6, -23.57) * mm, "end": v(33.46, -23.57) * mm});
            skArc(sketch, "E767", {"start": v(29.23, -19.43) * mm, "mid": v(30.78, -22.07) * mm, "end": v(33.46, -23.57) * mm});
            skLineSegment(sketch, "E768", {"start": v(29.23, -19.43) * mm, "end": v(29.23, 6.06) * mm});
            skArc(sketch, "E769", {"start": v(33.37, 10.16) * mm, "mid": v(30.63, 8.79) * mm, "end": v(29.23, 6.06) * mm});
            skLineSegment(sketch, "E770", {"start": v(33.37, 10.16) * mm, "end": v(58.77, 10.16) * mm});
            skArc(sketch, "E771", {"start": v(62.97, 6.03) * mm, "mid": v(61.44, 8.68) * mm, "end": v(58.77, 10.16) * mm});
            skCircle(sketch, "E772", {"center": v(45.99, 8.15) * mm, "radius": 1.56 * mm});
            skLineSegment(sketch, "E773", {"start": v(46.1, -3.05) * mm, "end": v(46.12, -5.86) * mm, "construction": true});
            skLineSegment(sketch, "E774", {"start": v(46.12, -5.86) * mm, "end": v(46.12, -23.57) * mm});
            skText(sketch, "E775", { "text": "Abby", "fontName": "OpenSans-Regular.ttf"});
            const initialGuessF0  = {"E94": [-0.0649, 0.01282, 1, 0, 0.00377], "E193": [-0.06219, -0.0225, 1, 0, 0.00377], "E290": [-0.02902, 0.0125, 1, 0, 0.00377], "E387": [-0.0301, -0.0225, 1, 0, 0.0037], "E484": [0.00813, 0.01242, 1, 0, 0.00225], "E581": [0.00398, -0.023, 1, 0, 0.00385], "E678": [0.03355, 0.01225, 1, 0, 0.0043], "E775": [0.04097, -0.0222, 1, 0, 0.00313]};
            skSetInitialGuess(sketch, initialGuessF0);
            skSolve(sketch);
        }
        {
            var Q0;
            Q0=makeQuery(id+"F0.imprint","IMPRINT",FACE,{"disambiguationData":[TD([[makeQuery(id+"F0.imprint","IMPRINT",EDGE,{"derivedFrom":sQuery(id+"F0.wireOp",EDGE,"E2")}),1.0]])]});
            var Q1;
            Q1=makeQuery(id+"F0.imprint","IMPRINT",FACE,{"disambiguationData":[TD([[makeQuery(id+"F0.imprint","IMPRINT",EDGE,{"derivedFrom":sQuery(id+"F0.wireOp",EDGE,"E99")}),1.0]])]});
            var Q2;
            Q2=makeQuery(id+"F0.imprint","IMPRINT",FACE,{"disambiguationData":[TD([[makeQuery(id+"F0.imprint","IMPRINT",EDGE,{"derivedFrom":sQuery(id+"F0.wireOp",EDGE,"E293")}),1.0]])]});
            var Q3;
            Q3=makeQuery(id+"F0.imprint","IMPRINT",FACE,{"disambiguationData":[TD([[makeQuery(id+"F0.imprint","IMPRINT",EDGE,{"derivedFrom":sQuery(id+"F0.wireOp",EDGE,"E390")}),1.0]])]});
            var Q4;
            Q4=makeQuery(id+"F0.imprint","IMPRINT",FACE,{"disambiguationData":[TD([[makeQuery(id+"F0.imprint","IMPRINT",EDGE,{"derivedFrom":sQuery(id+"F0.wireOp",EDGE,"E196")}),1.0]])]});
            var Q5;
            Q5=makeQuery(id+"F0.imprint","IMPRINT",FACE,{"disambiguationData":[TD([[makeQuery(id+"F0.imprint","IMPRINT",EDGE,{"derivedFrom":sQuery(id+"F0.wireOp",EDGE,"E487")}),1.0]])]});
            var Q6;
            Q6=makeQuery(id+"F0.imprint","IMPRINT",FACE,{"disambiguationData":[TD([[makeQuery(id+"F0.imprint","IMPRINT",EDGE,{"derivedFrom":sQuery(id+"F0.wireOp",EDGE,"E584")}),1.0]])]});
            extrude(context, id + "F1", {"entities" : qUnion([Q0, Q1, Q2, Q3, Q4, Q5, Q6]), "depth" : 2.54 * mm, "offsetDistance" : 25.4 * mm});
        }
        {
            var Q0;
            Q0=makeQuery(id+"F0.imprint","IMPRINT",FACE,{"disambiguationData":[TD([[makeQuery(id+"F0.imprint","IMPRINT",EDGE,{"derivedFrom":sQuery(id+"F0.wireOp",EDGE,"E2")}),-1.0]])]});
            var Q1;
            Q1=makeQuery(id+"F0.imprint","IMPRINT",FACE,{"disambiguationData":[TD([[makeQuery(id+"F0.imprint","IMPRINT",EDGE,{"derivedFrom":sQuery(id+"F0.wireOp",EDGE,"E99")}),-1.0]])]});
            var Q2;
            Q2=makeQuery(id+"F0.imprint","IMPRINT",FACE,{"disambiguationData":[TD([[makeQuery(id+"F0.imprint","IMPRINT",EDGE,{"derivedFrom":sQuery(id+"F0.wireOp",EDGE,"E196")}),-1.0]])]});
            var Q3;
            Q3=makeQuery(id+"F0.imprint","IMPRINT",FACE,{"disambiguationData":[TD([[makeQuery(id+"F0.imprint","IMPRINT",EDGE,{"derivedFrom":sQuery(id+"F0.wireOp",EDGE,"E293")}),-1.0]])]});
            var Q4;
            Q4=makeQuery(id+"F0.imprint","IMPRINT",FACE,{"disambiguationData":[TD([[makeQuery(id+"F0.imprint","IMPRINT",EDGE,{"derivedFrom":sQuery(id+"F0.wireOp",EDGE,"E487")}),-1.0]])]});
            var Q5;
            Q5=makeQuery(id+"F0.imprint","IMPRINT",FACE,{"disambiguationData":[TD([[makeQuery(id+"F0.imprint","IMPRINT",EDGE,{"derivedFrom":sQuery(id+"F0.wireOp",EDGE,"E390")}),-1.0]])]});
            var Q6;
            Q6=makeQuery(id+"F0.imprint","IMPRINT",FACE,{"disambiguationData":[TD([[makeQuery(id+"F0.imprint","IMPRINT",EDGE,{"derivedFrom":sQuery(id+"F0.wireOp",EDGE,"E584")}),-1.0]])]});
            extrude(context, id + "F2", {"entities" : qUnion([Q0, Q1, Q2, Q3, Q4, Q5, Q6]), "operationType" : NewBodyOperationType.ADD, "depth" : 1.27 * mm, "offsetDistance" : 25.4 * mm});
        }
    });
